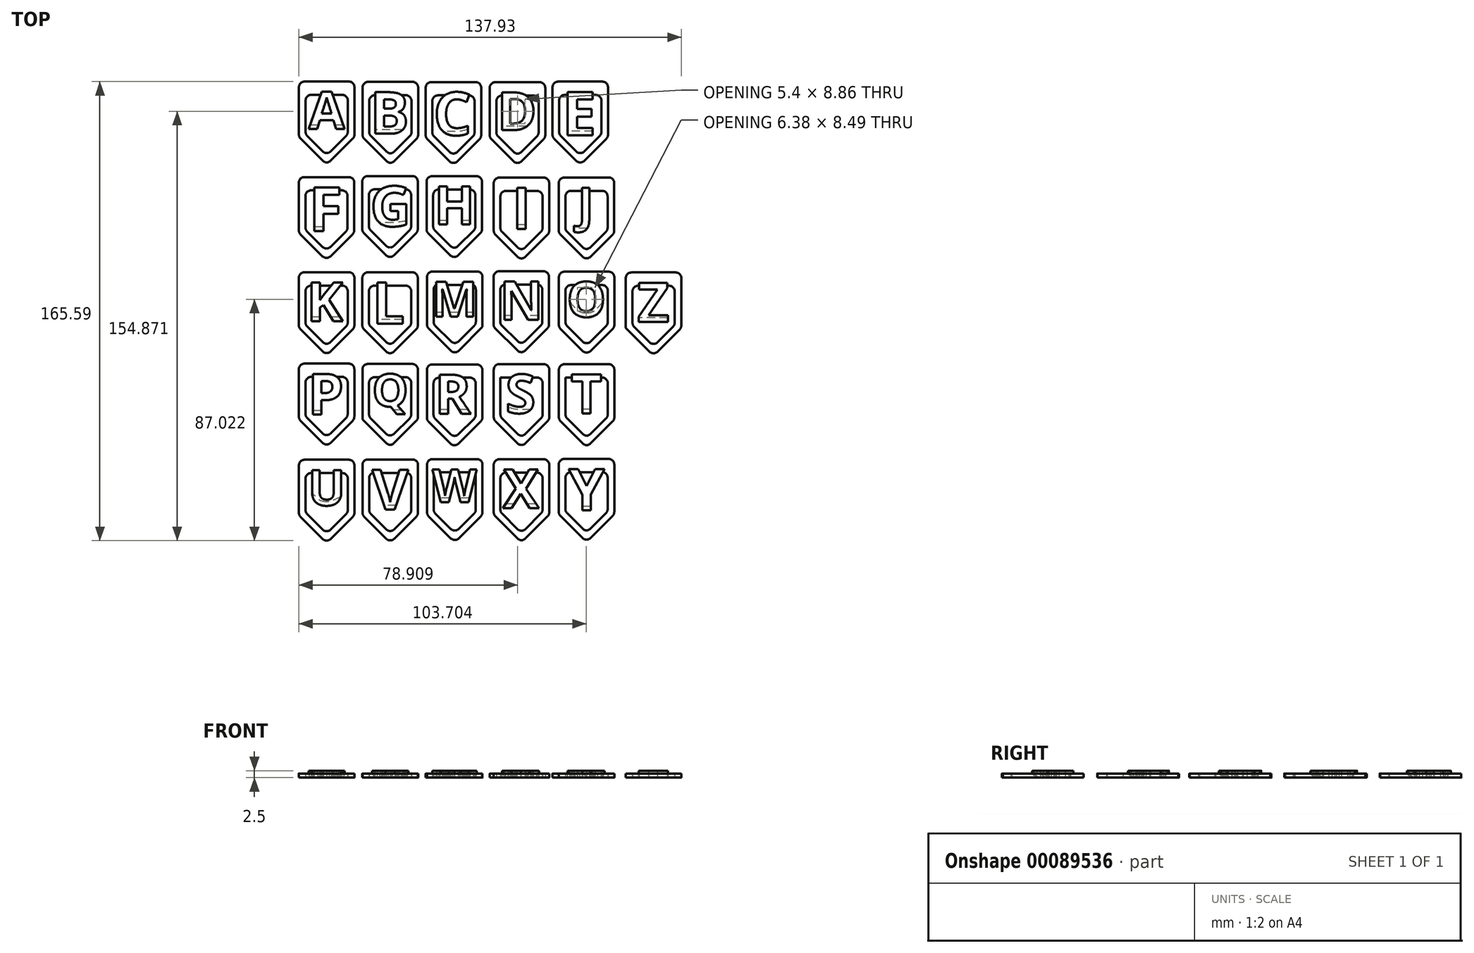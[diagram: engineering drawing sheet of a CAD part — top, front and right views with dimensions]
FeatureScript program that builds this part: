
annotation { "Feature Type Name" : "Feature", "Feature Type Description" : "" }
export const myFeature = defineFeature(function(context is Context, id is Id, definition is map)
    precondition{}
    {
        {
            assignVariable(context, id + "F0", {"name" : "ClipWidth", "anyValue" : 1.5});
        }
        {
            assignVariable(context, id + "F1", {"name" : "LetterWidth", "anyValue" : 2.5});
        }
        {
            var Q0;
            Q0=qCreatedBy(makeId("Top.planeOp"),FACE);
            var sketch = newSketch(context, id + "F2", { "sketchPlane" : qUnion([Q0])});
            skLineSegment(sketch, "E0", {"start": v(-68.8, 39.05) * mm, "end": v(-48.8, 39.05) * mm});
            skLineSegment(sketch, "E1", {"start": v(-48.8, 39.05) * mm, "end": v(-48.8, 19.05) * mm});
            skLineSegment(sketch, "E2", {"start": v(-48.8, 19.05) * mm, "end": v(-58.8, 9.05) * mm});
            skPoint(sketch, "E2.endSnap0", {"position": v(-58.8, 39.05) * mm});
            skLineSegment(sketch, "E3", {"start": v(-58.8, 9.05) * mm, "end": v(-68.8, 19.05) * mm});
            skLineSegment(sketch, "E4", {"start": v(-68.8, 19.05) * mm, "end": v(-68.8, 39.05) * mm});
            skLineSegment(sketch, "E5", {"start": v(-66.4, 34.25) * mm, "end": v(-51.2, 34.25) * mm});
            skLineSegment(sketch, "E6", {"start": v(-51.2, 34.25) * mm, "end": v(-51.2, 20.05) * mm});
            skLineSegment(sketch, "E7", {"start": v(-51.2, 20.05) * mm, "end": v(-58.8, 12.45) * mm});
            skLineSegment(sketch, "E8", {"start": v(-58.8, 12.45) * mm, "end": v(-66.4, 20.05) * mm});
            skLineSegment(sketch, "E9", {"start": v(-66.4, 20.05) * mm, "end": v(-66.4, 34.25) * mm});
            skText(sketch, "E10", { "text": "A", "fontName": "OpenSans-Bold.ttf"});
            skLineSegment(sketch, "E11", {"start": v(-58.8, 27.15) * mm, "end": v(-58.8, 43.75) * mm, "construction": true});
            const initialGuessF2  = {"E10": [-0.0653, 0.02189, 1, 0, 0.01357]};
            skSetInitialGuess(sketch, initialGuessF2);
            skSolve(sketch);
        }
        {
            var Q0;
            Q0=qCreatedBy(makeId("Top.planeOp"),FACE);
            var sketch = newSketch(context, id + "F3", { "sketchPlane" : qUnion([Q0])});
            skLineSegment(sketch, "E12", {"start": v(-45.83, 38.94) * mm, "end": v(-25.83, 38.94) * mm});
            skLineSegment(sketch, "E13", {"start": v(-25.83, 38.94) * mm, "end": v(-25.83, 18.94) * mm});
            skLineSegment(sketch, "E14", {"start": v(-25.83, 18.94) * mm, "end": v(-35.83, 8.94) * mm});
            skPoint(sketch, "E14.endSnap0", {"position": v(-35.83, 38.94) * mm});
            skLineSegment(sketch, "E15", {"start": v(-35.83, 8.94) * mm, "end": v(-45.83, 18.94) * mm});
            skLineSegment(sketch, "E16", {"start": v(-45.83, 18.94) * mm, "end": v(-45.83, 38.94) * mm});
            skLineSegment(sketch, "E17", {"start": v(-43.43, 34.14) * mm, "end": v(-28.23, 34.14) * mm});
            skLineSegment(sketch, "E18", {"start": v(-28.23, 34.14) * mm, "end": v(-28.23, 19.94) * mm});
            skLineSegment(sketch, "E19", {"start": v(-28.23, 19.94) * mm, "end": v(-35.83, 12.34) * mm});
            skLineSegment(sketch, "E20", {"start": v(-35.83, 12.34) * mm, "end": v(-43.43, 19.94) * mm});
            skLineSegment(sketch, "E21", {"start": v(-43.43, 19.94) * mm, "end": v(-43.43, 34.14) * mm});
            skText(sketch, "E22", { "text": "B", "fontName": "OpenSans-Bold.ttf"});
            skLineSegment(sketch, "E23", {"start": v(-35.83, 31.44) * mm, "end": v(-35.83, 39.25) * mm, "construction": true});
            const initialGuessF3  = {"E22": [-0.04323, 0.02023, 1, 0, 0.01512]};
            skSetInitialGuess(sketch, initialGuessF3);
            skSolve(sketch);
        }
        {
            var Q0;
            Q0=qCreatedBy(makeId("Top.planeOp"),FACE);
            var sketch = newSketch(context, id + "F4", { "sketchPlane" : qUnion([Q0])});
            skLineSegment(sketch, "E24", {"start": v(-23.1, 38.87) * mm, "end": v(-3.1, 38.87) * mm});
            skLineSegment(sketch, "E25", {"start": v(-3.1, 38.87) * mm, "end": v(-3.1, 18.87) * mm});
            skLineSegment(sketch, "E26", {"start": v(-3.1, 18.87) * mm, "end": v(-13.1, 8.87) * mm});
            skPoint(sketch, "E26.endSnap0", {"position": v(-13.1, 38.87) * mm});
            skLineSegment(sketch, "E27", {"start": v(-13.1, 8.87) * mm, "end": v(-23.1, 18.87) * mm});
            skLineSegment(sketch, "E28", {"start": v(-23.1, 18.87) * mm, "end": v(-23.1, 38.87) * mm});
            skLineSegment(sketch, "E29", {"start": v(-20.7, 34.07) * mm, "end": v(-5.5, 34.07) * mm});
            skLineSegment(sketch, "E30", {"start": v(-5.5, 34.07) * mm, "end": v(-5.5, 19.86) * mm});
            skLineSegment(sketch, "E31", {"start": v(-5.5, 19.86) * mm, "end": v(-13.1, 12.26) * mm});
            skLineSegment(sketch, "E32", {"start": v(-13.1, 12.26) * mm, "end": v(-20.7, 19.86) * mm});
            skLineSegment(sketch, "E33", {"start": v(-20.7, 19.86) * mm, "end": v(-20.7, 34.07) * mm});
            skText(sketch, "E34", { "text": "C", "fontName": "OpenSans-Bold.ttf"});
            skLineSegment(sketch, "E35", {"start": v(-13.1, 13.29) * mm, "end": v(-13.1, 57.25) * mm, "construction": true});
            const initialGuessF4  = {"E34": [-0.02035, 0.01972, 1, 0, 0.01555]};
            skSetInitialGuess(sketch, initialGuessF4);
            skSolve(sketch);
        }
        {
            var Q0;
            Q0=qCreatedBy(makeId("Top.planeOp"),FACE);
            var sketch = newSketch(context, id + "F5", { "sketchPlane" : qUnion([Q0])});
            skLineSegment(sketch, "E36", {"start": v(0, 38.85) * mm, "end": v(20, 38.85) * mm});
            skLineSegment(sketch, "E37", {"start": v(20, 38.85) * mm, "end": v(20, 18.85) * mm});
            skLineSegment(sketch, "E38", {"start": v(20, 18.85) * mm, "end": v(10, 8.85) * mm});
            skPoint(sketch, "E38.endSnap0", {"position": v(10, 38.85) * mm});
            skLineSegment(sketch, "E39", {"start": v(10, 8.85) * mm, "end": v(0, 18.85) * mm});
            skLineSegment(sketch, "E40", {"start": v(0, 18.85) * mm, "end": v(0, 38.85) * mm});
            skLineSegment(sketch, "E41", {"start": v(2.4, 34.05) * mm, "end": v(17.6, 34.05) * mm});
            skLineSegment(sketch, "E42", {"start": v(17.6, 34.05) * mm, "end": v(17.6, 19.84) * mm});
            skLineSegment(sketch, "E43", {"start": v(17.6, 19.84) * mm, "end": v(10, 12.24) * mm});
            skLineSegment(sketch, "E44", {"start": v(10, 12.24) * mm, "end": v(2.4, 19.84) * mm});
            skLineSegment(sketch, "E45", {"start": v(2.4, 19.84) * mm, "end": v(2.4, 34.05) * mm});
            skText(sketch, "E46", { "text": "D", "fontName": "OpenSans-Bold.ttf"});
            skLineSegment(sketch, "E47", {"start": v(10, 0.42) * mm, "end": v(10, 70.07) * mm, "construction": true});
            const initialGuessF5  = {"E46": [0.00275, 0.02152, 1, 0, 0.01372]};
            skSetInitialGuess(sketch, initialGuessF5);
            skSolve(sketch);
        }
        {
            var Q0;
            Q0=qCreatedBy(makeId("Top.planeOp"),FACE);
            var sketch = newSketch(context, id + "F6", { "sketchPlane" : qUnion([Q0])});
            skLineSegment(sketch, "E48", {"start": v(22.63, 39.03) * mm, "end": v(42.63, 39.03) * mm});
            skLineSegment(sketch, "E49", {"start": v(42.63, 39.03) * mm, "end": v(42.63, 19.03) * mm});
            skLineSegment(sketch, "E50", {"start": v(42.63, 19.03) * mm, "end": v(32.63, 9.03) * mm});
            skPoint(sketch, "E50.endSnap0", {"position": v(32.63, 39.03) * mm});
            skLineSegment(sketch, "E51", {"start": v(32.63, 9.03) * mm, "end": v(22.63, 19.03) * mm});
            skLineSegment(sketch, "E52", {"start": v(22.63, 19.03) * mm, "end": v(22.63, 39.03) * mm});
            skLineSegment(sketch, "E53", {"start": v(25.03, 34.23) * mm, "end": v(40.23, 34.23) * mm});
            skLineSegment(sketch, "E54", {"start": v(40.23, 34.23) * mm, "end": v(40.23, 20.02) * mm});
            skLineSegment(sketch, "E55", {"start": v(40.23, 20.02) * mm, "end": v(32.63, 12.42) * mm});
            skLineSegment(sketch, "E56", {"start": v(32.63, 12.42) * mm, "end": v(25.03, 20.02) * mm});
            skLineSegment(sketch, "E57", {"start": v(25.03, 20.02) * mm, "end": v(25.03, 34.23) * mm});
            skText(sketch, "E58", { "text": "E", "fontName": "OpenSans-Bold.ttf"});
            skLineSegment(sketch, "E59", {"start": v(32.63, 0.42) * mm, "end": v(32.63, 70.43) * mm, "construction": true});
            const initialGuessF6  = {"E58": [0.02614, 0.01962, 1, 0, 0.01581]};
            skSetInitialGuess(sketch, initialGuessF6);
            skSolve(sketch);
        }
        {
            var Q0;
            Q0=qCreatedBy(makeId("Top.planeOp"),FACE);
            var sketch = newSketch(context, id + "F7", { "sketchPlane" : qUnion([Q0])});
            skLineSegment(sketch, "E60", {"start": v(-68.86, 4.6) * mm, "end": v(-48.86, 4.6) * mm});
            skLineSegment(sketch, "E61", {"start": v(-48.86, 4.6) * mm, "end": v(-48.86, -15.4) * mm});
            skLineSegment(sketch, "E62", {"start": v(-48.86, -15.4) * mm, "end": v(-58.86, -25.4) * mm});
            skPoint(sketch, "E62.endSnap0", {"position": v(-58.86, 4.6) * mm});
            skLineSegment(sketch, "E63", {"start": v(-58.86, -25.4) * mm, "end": v(-68.86, -15.4) * mm});
            skLineSegment(sketch, "E64", {"start": v(-68.86, -15.4) * mm, "end": v(-68.86, 4.6) * mm});
            skLineSegment(sketch, "E65", {"start": v(-66.46, -0.2) * mm, "end": v(-51.26, -0.2) * mm});
            skLineSegment(sketch, "E66", {"start": v(-51.26, -0.2) * mm, "end": v(-51.26, -14.4) * mm});
            skLineSegment(sketch, "E67", {"start": v(-51.26, -14.4) * mm, "end": v(-58.86, -22) * mm});
            skLineSegment(sketch, "E68", {"start": v(-58.86, -22) * mm, "end": v(-66.46, -14.4) * mm});
            skLineSegment(sketch, "E69", {"start": v(-66.46, -14.4) * mm, "end": v(-66.46, -0.2) * mm});
            skText(sketch, "E70", { "text": "F", "fontName": "OpenSans-Bold.ttf"});
            skLineSegment(sketch, "E71", {"start": v(-58.86, -29.54) * mm, "end": v(-58.86, 31.53) * mm, "construction": true});
            const initialGuessF7  = {"E70": [-0.0652, -0.01487, 1, 0, 0.01587]};
            skSetInitialGuess(sketch, initialGuessF7);
            skSolve(sketch);
        }
        {
            var Q0;
            Q0=qCreatedBy(makeId("Top.planeOp"),FACE);
            var sketch = newSketch(context, id + "F8", { "sketchPlane" : qUnion([Q0])});
            skLineSegment(sketch, "E72", {"start": v(-45.95, 4.98) * mm, "end": v(-25.95, 4.98) * mm});
            skLineSegment(sketch, "E73", {"start": v(-25.95, 4.98) * mm, "end": v(-25.95, -15.02) * mm});
            skLineSegment(sketch, "E74", {"start": v(-25.95, -15.02) * mm, "end": v(-35.95, -25.02) * mm});
            skPoint(sketch, "E74.endSnap0", {"position": v(-35.95, 4.98) * mm});
            skLineSegment(sketch, "E75", {"start": v(-35.95, -25.02) * mm, "end": v(-45.95, -15.02) * mm});
            skLineSegment(sketch, "E76", {"start": v(-45.95, -15.02) * mm, "end": v(-45.95, 4.98) * mm});
            skLineSegment(sketch, "E77", {"start": v(-43.55, 0.18) * mm, "end": v(-28.35, 0.18) * mm});
            skLineSegment(sketch, "E78", {"start": v(-28.35, 0.18) * mm, "end": v(-28.35, -14.02) * mm});
            skLineSegment(sketch, "E79", {"start": v(-28.35, -14.02) * mm, "end": v(-35.95, -21.62) * mm});
            skLineSegment(sketch, "E80", {"start": v(-35.95, -21.62) * mm, "end": v(-43.55, -14.02) * mm});
            skLineSegment(sketch, "E81", {"start": v(-43.55, -14.02) * mm, "end": v(-43.55, 0.18) * mm});
            skText(sketch, "E82", { "text": "G", "fontName": "OpenSans-Bold.ttf"});
            skLineSegment(sketch, "E83", {"start": v(-35.95, -0.1) * mm, "end": v(-35.95, 2.87) * mm, "construction": true});
            const initialGuessF8  = {"E82": [-0.0431, -0.01315, 1, 0, 0.01453]};
            skSetInitialGuess(sketch, initialGuessF8);
            skSolve(sketch);
        }
        {
            var Q0;
            Q0=qCreatedBy(makeId("Top.planeOp"),FACE);
            var sketch = newSketch(context, id + "F9", { "sketchPlane" : qUnion([Q0])});
            skLineSegment(sketch, "E84", {"start": v(-22.8, 4.94) * mm, "end": v(-2.8, 4.94) * mm});
            skLineSegment(sketch, "E85", {"start": v(-2.8, 4.94) * mm, "end": v(-2.8, -15.06) * mm});
            skLineSegment(sketch, "E86", {"start": v(-2.8, -15.06) * mm, "end": v(-12.8, -25.06) * mm});
            skPoint(sketch, "E86.endSnap0", {"position": v(-12.8, 4.94) * mm});
            skLineSegment(sketch, "E87", {"start": v(-12.8, -25.06) * mm, "end": v(-22.8, -15.06) * mm});
            skLineSegment(sketch, "E88", {"start": v(-22.8, -15.06) * mm, "end": v(-22.8, 4.94) * mm});
            skLineSegment(sketch, "E89", {"start": v(-20.4, 0.14) * mm, "end": v(-5.2, 0.14) * mm});
            skLineSegment(sketch, "E90", {"start": v(-5.2, 0.14) * mm, "end": v(-5.2, -14.07) * mm});
            skLineSegment(sketch, "E91", {"start": v(-5.2, -14.07) * mm, "end": v(-12.8, -21.67) * mm});
            skLineSegment(sketch, "E92", {"start": v(-12.8, -21.67) * mm, "end": v(-20.4, -14.07) * mm});
            skLineSegment(sketch, "E93", {"start": v(-20.4, -14.07) * mm, "end": v(-20.4, 0.14) * mm});
            skText(sketch, "E94", { "text": "H", "fontName": "OpenSans-Bold.ttf"});
            skLineSegment(sketch, "E95", {"start": v(-12.8, 0.84) * mm, "end": v(-12.8, 1.84) * mm, "construction": true});
            const initialGuessF9  = {"E94": [-0.02007, -0.01253, 1, 0, 0.01387]};
            skSetInitialGuess(sketch, initialGuessF9);
            skSolve(sketch);
        }
        {
            var Q0;
            Q0=qCreatedBy(makeId("Top.planeOp"),FACE);
            var sketch = newSketch(context, id + "F10", { "sketchPlane" : qUnion([Q0])});
            skLineSegment(sketch, "E96", {"start": v(1.43, 4.42) * mm, "end": v(21.43, 4.42) * mm});
            skLineSegment(sketch, "E97", {"start": v(21.43, 4.42) * mm, "end": v(21.43, -15.58) * mm});
            skLineSegment(sketch, "E98", {"start": v(21.43, -15.58) * mm, "end": v(11.43, -25.58) * mm});
            skPoint(sketch, "E98.endSnap0", {"position": v(11.43, 4.42) * mm});
            skLineSegment(sketch, "E99", {"start": v(11.43, -25.58) * mm, "end": v(1.43, -15.58) * mm});
            skLineSegment(sketch, "E100", {"start": v(1.43, -15.58) * mm, "end": v(1.43, 4.42) * mm});
            skLineSegment(sketch, "E101", {"start": v(3.83, -0.38) * mm, "end": v(19.03, -0.38) * mm});
            skLineSegment(sketch, "E102", {"start": v(19.03, -0.38) * mm, "end": v(19.03, -14.59) * mm});
            skLineSegment(sketch, "E103", {"start": v(19.03, -14.59) * mm, "end": v(11.43, -22.19) * mm});
            skLineSegment(sketch, "E104", {"start": v(11.43, -22.19) * mm, "end": v(3.83, -14.59) * mm});
            skLineSegment(sketch, "E105", {"start": v(3.83, -14.59) * mm, "end": v(3.83, -0.38) * mm});
            skText(sketch, "E106", { "text": "I", "fontName": "OpenSans-Bold.ttf"});
            skLineSegment(sketch, "E107", {"start": v(11.43, -0.98) * mm, "end": v(11.43, 3.5) * mm, "construction": true});
            const initialGuessF10  = {"E106": [0.00798, -0.0141, 1, 0, 0.01492]};
            skSetInitialGuess(sketch, initialGuessF10);
            skSolve(sketch);
        }
        {
            var Q0;
            Q0=qCreatedBy(makeId("Top.planeOp"),FACE);
            var sketch = newSketch(context, id + "F11", { "sketchPlane" : qUnion([Q0])});
            skLineSegment(sketch, "E108", {"start": v(24.89, 4.45) * mm, "end": v(44.89, 4.45) * mm});
            skLineSegment(sketch, "E109", {"start": v(44.89, 4.45) * mm, "end": v(44.89, -15.55) * mm});
            skLineSegment(sketch, "E110", {"start": v(44.89, -15.55) * mm, "end": v(34.89, -25.55) * mm});
            skPoint(sketch, "E110.endSnap0", {"position": v(34.89, 4.45) * mm});
            skLineSegment(sketch, "E111", {"start": v(34.89, -25.55) * mm, "end": v(24.89, -15.55) * mm});
            skLineSegment(sketch, "E112", {"start": v(24.89, -15.55) * mm, "end": v(24.89, 4.45) * mm});
            skLineSegment(sketch, "E113", {"start": v(27.29, -0.35) * mm, "end": v(42.49, -0.35) * mm});
            skLineSegment(sketch, "E114", {"start": v(42.49, -0.35) * mm, "end": v(42.49, -14.55) * mm});
            skLineSegment(sketch, "E115", {"start": v(42.49, -14.55) * mm, "end": v(34.89, -22.15) * mm});
            skLineSegment(sketch, "E116", {"start": v(34.89, -22.15) * mm, "end": v(27.29, -14.55) * mm});
            skLineSegment(sketch, "E117", {"start": v(27.29, -14.55) * mm, "end": v(27.29, -0.35) * mm});
            skText(sketch, "E118", { "text": "J", "fontName": "OpenSans-Bold.ttf"});
            skLineSegment(sketch, "E119", {"start": v(34.89, -5.18) * mm, "end": v(34.89, 6.88) * mm, "construction": true});
            const initialGuessF11  = {"E118": [0.03168, -0.0117, 1, 0, 0.01255]};
            skSetInitialGuess(sketch, initialGuessF11);
            skSolve(sketch);
        }
        {
            var Q0;
            Q0=qCreatedBy(makeId("Top.planeOp"),FACE);
            var sketch = newSketch(context, id + "F12", { "sketchPlane" : qUnion([Q0])});
            skLineSegment(sketch, "E120", {"start": v(-68.82, -29.73) * mm, "end": v(-48.82, -29.73) * mm});
            skLineSegment(sketch, "E121", {"start": v(-48.82, -29.73) * mm, "end": v(-48.82, -49.73) * mm});
            skLineSegment(sketch, "E122", {"start": v(-48.82, -49.73) * mm, "end": v(-58.82, -59.73) * mm});
            skPoint(sketch, "E122.endSnap0", {"position": v(-58.82, -29.73) * mm});
            skLineSegment(sketch, "E123", {"start": v(-58.82, -59.73) * mm, "end": v(-68.82, -49.73) * mm});
            skLineSegment(sketch, "E124", {"start": v(-68.82, -49.73) * mm, "end": v(-68.82, -29.73) * mm});
            skLineSegment(sketch, "E125", {"start": v(-66.42, -34.53) * mm, "end": v(-51.22, -34.53) * mm});
            skLineSegment(sketch, "E126", {"start": v(-51.22, -34.53) * mm, "end": v(-51.22, -48.73) * mm});
            skLineSegment(sketch, "E127", {"start": v(-51.22, -48.73) * mm, "end": v(-58.82, -56.33) * mm});
            skLineSegment(sketch, "E128", {"start": v(-58.82, -56.33) * mm, "end": v(-66.42, -48.73) * mm});
            skLineSegment(sketch, "E129", {"start": v(-66.42, -48.73) * mm, "end": v(-66.42, -34.53) * mm});
            skText(sketch, "E130", { "text": "K", "fontName": "OpenSans-Bold.ttf"});
            skLineSegment(sketch, "E131", {"start": v(-58.82, -47.23) * mm, "end": v(-58.82, -19.43) * mm, "construction": true});
            const initialGuessF12  = {"E130": [-0.06598, -0.04742, 1, 0, 0.0141]};
            skSetInitialGuess(sketch, initialGuessF12);
            skSolve(sketch);
        }
        {
            var Q0;
            Q0=qCreatedBy(makeId("Top.planeOp"),FACE);
            var sketch = newSketch(context, id + "F13", { "sketchPlane" : qUnion([Q0])});
            skLineSegment(sketch, "E132", {"start": v(-45.94, -29.75) * mm, "end": v(-25.94, -29.75) * mm});
            skLineSegment(sketch, "E133", {"start": v(-25.94, -29.75) * mm, "end": v(-25.94, -49.75) * mm});
            skLineSegment(sketch, "E134", {"start": v(-25.94, -49.75) * mm, "end": v(-35.94, -59.75) * mm});
            skPoint(sketch, "E134.endSnap0", {"position": v(-35.94, -29.75) * mm});
            skLineSegment(sketch, "E135", {"start": v(-35.94, -59.75) * mm, "end": v(-45.94, -49.75) * mm});
            skLineSegment(sketch, "E136", {"start": v(-45.94, -49.75) * mm, "end": v(-45.94, -29.75) * mm});
            skLineSegment(sketch, "E137", {"start": v(-43.54, -34.55) * mm, "end": v(-28.34, -34.55) * mm});
            skLineSegment(sketch, "E138", {"start": v(-28.34, -34.55) * mm, "end": v(-28.34, -48.76) * mm});
            skLineSegment(sketch, "E139", {"start": v(-28.34, -48.76) * mm, "end": v(-35.94, -56.36) * mm});
            skLineSegment(sketch, "E140", {"start": v(-35.94, -56.36) * mm, "end": v(-43.54, -48.76) * mm});
            skLineSegment(sketch, "E141", {"start": v(-43.54, -48.76) * mm, "end": v(-43.54, -34.55) * mm});
            skText(sketch, "E142", { "text": "L", "fontName": "OpenSans-Bold.ttf"});
            skLineSegment(sketch, "E143", {"start": v(-35.94, -40.7) * mm, "end": v(-35.94, -26) * mm, "construction": true});
            const initialGuessF13  = {"E142": [-0.04236, -0.04827, 1, 0, 0.01492]};
            skSetInitialGuess(sketch, initialGuessF13);
            skSolve(sketch);
        }
        {
            var Q0;
            Q0=qCreatedBy(makeId("Top.planeOp"),FACE);
            var sketch = newSketch(context, id + "F14", { "sketchPlane" : qUnion([Q0])});
            skLineSegment(sketch, "E144", {"start": v(-22.62, -29.46) * mm, "end": v(-2.62, -29.46) * mm});
            skLineSegment(sketch, "E145", {"start": v(-2.62, -29.46) * mm, "end": v(-2.62, -49.46) * mm});
            skLineSegment(sketch, "E146", {"start": v(-2.62, -49.46) * mm, "end": v(-12.62, -59.46) * mm});
            skPoint(sketch, "E146.endSnap0", {"position": v(-12.62, -29.46) * mm});
            skLineSegment(sketch, "E147", {"start": v(-12.62, -59.46) * mm, "end": v(-22.62, -49.46) * mm});
            skLineSegment(sketch, "E148", {"start": v(-22.62, -49.46) * mm, "end": v(-22.62, -29.46) * mm});
            skLineSegment(sketch, "E149", {"start": v(-20.22, -34.26) * mm, "end": v(-5.02, -34.26) * mm});
            skLineSegment(sketch, "E150", {"start": v(-5.02, -34.26) * mm, "end": v(-5.02, -48.46) * mm});
            skLineSegment(sketch, "E151", {"start": v(-5.02, -48.46) * mm, "end": v(-12.62, -56.06) * mm});
            skLineSegment(sketch, "E152", {"start": v(-12.62, -56.06) * mm, "end": v(-20.22, -48.46) * mm});
            skLineSegment(sketch, "E153", {"start": v(-20.22, -48.46) * mm, "end": v(-20.22, -34.26) * mm});
            skText(sketch, "E154", { "text": "M", "fontName": "OpenSans-Bold.ttf"});
            skLineSegment(sketch, "E155", {"start": v(-12.62, -42.78) * mm, "end": v(-12.62, -23.34) * mm, "construction": true});
            const initialGuessF14  = {"E154": [-0.02094, -0.04572, 1, 0, 0.01266]};
            skSetInitialGuess(sketch, initialGuessF14);
            skSolve(sketch);
        }
        {
            var Q0;
            Q0=qCreatedBy(makeId("Top.planeOp"),FACE);
            var sketch = newSketch(context, id + "F15", { "sketchPlane" : qUnion([Q0])});
            skLineSegment(sketch, "E156", {"start": v(1.38, -29.38) * mm, "end": v(21.38, -29.38) * mm});
            skLineSegment(sketch, "E157", {"start": v(21.38, -29.38) * mm, "end": v(21.38, -49.38) * mm});
            skLineSegment(sketch, "E158", {"start": v(21.38, -49.38) * mm, "end": v(11.38, -59.38) * mm});
            skPoint(sketch, "E158.endSnap0", {"position": v(11.38, -29.38) * mm});
            skLineSegment(sketch, "E159", {"start": v(11.38, -59.38) * mm, "end": v(1.38, -49.38) * mm});
            skLineSegment(sketch, "E160", {"start": v(1.38, -49.38) * mm, "end": v(1.38, -29.38) * mm});
            skLineSegment(sketch, "E161", {"start": v(3.78, -34.18) * mm, "end": v(18.98, -34.18) * mm});
            skLineSegment(sketch, "E162", {"start": v(18.98, -34.18) * mm, "end": v(18.98, -48.38) * mm});
            skLineSegment(sketch, "E163", {"start": v(18.98, -48.38) * mm, "end": v(11.38, -55.98) * mm});
            skLineSegment(sketch, "E164", {"start": v(11.38, -55.98) * mm, "end": v(3.78, -48.38) * mm});
            skLineSegment(sketch, "E165", {"start": v(3.78, -48.38) * mm, "end": v(3.78, -34.18) * mm});
            skText(sketch, "E166", { "text": "N", "fontName": "OpenSans-Bold.ttf"});
            skLineSegment(sketch, "E167", {"start": v(11.38, -50.26) * mm, "end": v(11.38, -15.7) * mm, "construction": true});
            const initialGuessF15  = {"E166": [0.00354, -0.04691, 1, 0, 0.01394]};
            skSetInitialGuess(sketch, initialGuessF15);
            skSolve(sketch);
        }
        {
            var Q0;
            Q0=qCreatedBy(makeId("Top.planeOp"),FACE);
            var sketch = newSketch(context, id + "F16", { "sketchPlane" : qUnion([Q0])});
            skLineSegment(sketch, "E168", {"start": v(24.92, -29.55) * mm, "end": v(44.92, -29.55) * mm});
            skLineSegment(sketch, "E169", {"start": v(44.92, -29.55) * mm, "end": v(44.92, -49.55) * mm});
            skLineSegment(sketch, "E170", {"start": v(44.92, -49.55) * mm, "end": v(34.92, -59.55) * mm});
            skPoint(sketch, "E170.endSnap0", {"position": v(34.92, -29.55) * mm});
            skLineSegment(sketch, "E171", {"start": v(34.92, -59.55) * mm, "end": v(24.92, -49.55) * mm});
            skLineSegment(sketch, "E172", {"start": v(24.92, -49.55) * mm, "end": v(24.92, -29.55) * mm});
            skLineSegment(sketch, "E173", {"start": v(27.32, -34.35) * mm, "end": v(42.52, -34.35) * mm});
            skLineSegment(sketch, "E174", {"start": v(42.52, -34.35) * mm, "end": v(42.52, -48.55) * mm});
            skLineSegment(sketch, "E175", {"start": v(42.52, -48.55) * mm, "end": v(34.92, -56.15) * mm});
            skLineSegment(sketch, "E176", {"start": v(34.92, -56.15) * mm, "end": v(27.32, -48.55) * mm});
            skLineSegment(sketch, "E177", {"start": v(27.32, -48.55) * mm, "end": v(27.32, -34.35) * mm});
            skText(sketch, "E178", { "text": "O", "fontName": "OpenSans-Bold.ttf"});
            skLineSegment(sketch, "E179", {"start": v(34.92, -52.38) * mm, "end": v(34.92, -13.92) * mm, "construction": true});
            const initialGuessF16  = {"E178": [0.02783, -0.04583, 1, 0, 0.01269]};
            skSetInitialGuess(sketch, initialGuessF16);
            skSolve(sketch);
        }
        {
            var Q0;
            Q0=qCreatedBy(makeId("Top.planeOp"),FACE);
            var sketch = newSketch(context, id + "F17", { "sketchPlane" : qUnion([Q0])});
            skLineSegment(sketch, "E180", {"start": v(-68.83, -62.7) * mm, "end": v(-48.83, -62.7) * mm});
            skLineSegment(sketch, "E181", {"start": v(-48.83, -62.7) * mm, "end": v(-48.83, -82.7) * mm});
            skLineSegment(sketch, "E182", {"start": v(-48.83, -82.7) * mm, "end": v(-58.83, -92.7) * mm});
            skPoint(sketch, "E182.endSnap0", {"position": v(-58.83, -62.7) * mm});
            skLineSegment(sketch, "E183", {"start": v(-58.83, -92.7) * mm, "end": v(-68.83, -82.7) * mm});
            skLineSegment(sketch, "E184", {"start": v(-68.83, -82.7) * mm, "end": v(-68.83, -62.7) * mm});
            skLineSegment(sketch, "E185", {"start": v(-66.43, -67.5) * mm, "end": v(-51.23, -67.5) * mm});
            skLineSegment(sketch, "E186", {"start": v(-51.23, -67.5) * mm, "end": v(-51.23, -81.7) * mm});
            skLineSegment(sketch, "E187", {"start": v(-51.23, -81.7) * mm, "end": v(-58.83, -89.3) * mm});
            skLineSegment(sketch, "E188", {"start": v(-58.83, -89.3) * mm, "end": v(-66.43, -81.7) * mm});
            skLineSegment(sketch, "E189", {"start": v(-66.43, -81.7) * mm, "end": v(-66.43, -67.5) * mm});
            skText(sketch, "E190", { "text": "P", "fontName": "OpenSans-Bold.ttf"});
            skLineSegment(sketch, "E191", {"start": v(-58.83, -82.94) * mm, "end": v(-58.83, -49.65) * mm, "construction": true});
            const initialGuessF17  = {"E190": [-0.06562, -0.08111, 1, 0, 0.01482]};
            skSetInitialGuess(sketch, initialGuessF17);
            skSolve(sketch);
        }
        {
            var Q0;
            Q0=qCreatedBy(makeId("Top.planeOp"),FACE);
            var sketch = newSketch(context, id + "F18", { "sketchPlane" : qUnion([Q0])});
            skLineSegment(sketch, "E192", {"start": v(-45.91, -62.8) * mm, "end": v(-25.91, -62.8) * mm});
            skLineSegment(sketch, "E193", {"start": v(-25.91, -62.8) * mm, "end": v(-25.91, -82.8) * mm});
            skLineSegment(sketch, "E194", {"start": v(-25.91, -82.8) * mm, "end": v(-35.91, -92.8) * mm});
            skPoint(sketch, "E194.endSnap0", {"position": v(-35.91, -62.8) * mm});
            skLineSegment(sketch, "E195", {"start": v(-35.91, -92.8) * mm, "end": v(-45.91, -82.8) * mm});
            skLineSegment(sketch, "E196", {"start": v(-45.91, -82.8) * mm, "end": v(-45.91, -62.8) * mm});
            skLineSegment(sketch, "E197", {"start": v(-43.51, -67.6) * mm, "end": v(-28.31, -67.6) * mm});
            skLineSegment(sketch, "E198", {"start": v(-28.31, -67.6) * mm, "end": v(-28.31, -81.82) * mm});
            skLineSegment(sketch, "E199", {"start": v(-28.31, -81.82) * mm, "end": v(-35.91, -89.42) * mm});
            skLineSegment(sketch, "E200", {"start": v(-35.91, -89.42) * mm, "end": v(-43.51, -81.82) * mm});
            skLineSegment(sketch, "E201", {"start": v(-43.51, -81.82) * mm, "end": v(-43.51, -67.6) * mm});
            skText(sketch, "E202", { "text": "Q", "fontName": "OpenSans-Bold.ttf"});
            skLineSegment(sketch, "E203", {"start": v(-35.91, -81.8) * mm, "end": v(-35.91, -51.02) * mm, "construction": true});
            const initialGuessF18  = {"E202": [-0.04237, -0.07812, 1, 0, 0.01171]};
            skSetInitialGuess(sketch, initialGuessF18);
            skSolve(sketch);
        }
        {
            var Q0;
            Q0=qCreatedBy(makeId("Top.planeOp"),FACE);
            var sketch = newSketch(context, id + "F19", { "sketchPlane" : qUnion([Q0])});
            skLineSegment(sketch, "E204", {"start": v(-22.67, -62.97) * mm, "end": v(-2.67, -62.97) * mm});
            skLineSegment(sketch, "E205", {"start": v(-2.67, -62.97) * mm, "end": v(-2.67, -82.97) * mm});
            skLineSegment(sketch, "E206", {"start": v(-2.67, -82.97) * mm, "end": v(-12.67, -92.97) * mm});
            skPoint(sketch, "E206.endSnap0", {"position": v(-12.67, -62.97) * mm});
            skLineSegment(sketch, "E207", {"start": v(-12.67, -92.97) * mm, "end": v(-22.67, -82.97) * mm});
            skLineSegment(sketch, "E208", {"start": v(-22.67, -82.97) * mm, "end": v(-22.67, -62.97) * mm});
            skLineSegment(sketch, "E209", {"start": v(-20.27, -67.77) * mm, "end": v(-5.07, -67.77) * mm});
            skLineSegment(sketch, "E210", {"start": v(-5.07, -67.77) * mm, "end": v(-5.07, -81.98) * mm});
            skLineSegment(sketch, "E211", {"start": v(-5.07, -81.98) * mm, "end": v(-12.67, -89.58) * mm});
            skLineSegment(sketch, "E212", {"start": v(-12.67, -89.58) * mm, "end": v(-20.27, -81.98) * mm});
            skLineSegment(sketch, "E213", {"start": v(-20.27, -81.98) * mm, "end": v(-20.27, -67.77) * mm});
            skText(sketch, "E214", { "text": "R", "fontName": "OpenSans-Bold.ttf"});
            skLineSegment(sketch, "E215", {"start": v(-12.67, -86.91) * mm, "end": v(-12.67, -46.23) * mm, "construction": true});
            const initialGuessF19  = {"E214": [-0.0198, -0.08075, 1, 0, 0.01418]};
            skSetInitialGuess(sketch, initialGuessF19);
            skSolve(sketch);
        }
        {
            var Q0;
            Q0=qCreatedBy(makeId("Top.planeOp"),FACE);
            var sketch = newSketch(context, id + "F20", { "sketchPlane" : qUnion([Q0])});
            skLineSegment(sketch, "E216", {"start": v(1.45, -62.87) * mm, "end": v(21.45, -62.87) * mm});
            skLineSegment(sketch, "E217", {"start": v(21.45, -62.87) * mm, "end": v(21.45, -82.87) * mm});
            skLineSegment(sketch, "E218", {"start": v(21.45, -82.87) * mm, "end": v(11.45, -92.87) * mm});
            skPoint(sketch, "E218.endSnap0", {"position": v(11.45, -62.87) * mm});
            skLineSegment(sketch, "E219", {"start": v(11.45, -92.87) * mm, "end": v(1.45, -82.87) * mm});
            skLineSegment(sketch, "E220", {"start": v(1.45, -82.87) * mm, "end": v(1.45, -62.87) * mm});
            skLineSegment(sketch, "E221", {"start": v(3.85, -67.67) * mm, "end": v(19.05, -67.67) * mm});
            skLineSegment(sketch, "E222", {"start": v(19.05, -67.67) * mm, "end": v(19.05, -81.88) * mm});
            skLineSegment(sketch, "E223", {"start": v(19.05, -81.88) * mm, "end": v(11.45, -89.48) * mm});
            skLineSegment(sketch, "E224", {"start": v(11.45, -89.48) * mm, "end": v(3.85, -81.88) * mm});
            skLineSegment(sketch, "E225", {"start": v(3.85, -81.88) * mm, "end": v(3.85, -67.67) * mm});
            skText(sketch, "E226", { "text": "S", "fontName": "OpenSans-Bold.ttf"});
            skLineSegment(sketch, "E227", {"start": v(11.45, -80.26) * mm, "end": v(11.45, -52.69) * mm, "construction": true});
            const initialGuessF20  = {"E226": [0.00571, -0.08056, 1, 0, 0.01408]};
            skSetInitialGuess(sketch, initialGuessF20);
            skSolve(sketch);
        }
        {
            var Q0;
            Q0=qCreatedBy(makeId("Top.planeOp"),FACE);
            var sketch = newSketch(context, id + "F21", { "sketchPlane" : qUnion([Q0])});
            skLineSegment(sketch, "E228", {"start": v(24.93, -62.91) * mm, "end": v(44.93, -62.91) * mm});
            skLineSegment(sketch, "E229", {"start": v(44.93, -62.91) * mm, "end": v(44.93, -82.91) * mm});
            skLineSegment(sketch, "E230", {"start": v(44.93, -82.91) * mm, "end": v(34.93, -92.91) * mm});
            skPoint(sketch, "E230.endSnap0", {"position": v(34.93, -62.91) * mm});
            skLineSegment(sketch, "E231", {"start": v(34.93, -92.91) * mm, "end": v(24.93, -82.91) * mm});
            skLineSegment(sketch, "E232", {"start": v(24.93, -82.91) * mm, "end": v(24.93, -62.91) * mm});
            skLineSegment(sketch, "E233", {"start": v(27.33, -67.71) * mm, "end": v(42.53, -67.71) * mm});
            skLineSegment(sketch, "E234", {"start": v(42.53, -67.71) * mm, "end": v(42.53, -81.92) * mm});
            skLineSegment(sketch, "E235", {"start": v(42.53, -81.92) * mm, "end": v(34.93, -89.52) * mm});
            skLineSegment(sketch, "E236", {"start": v(34.93, -89.52) * mm, "end": v(27.33, -81.92) * mm});
            skLineSegment(sketch, "E237", {"start": v(27.33, -81.92) * mm, "end": v(27.33, -67.71) * mm});
            skText(sketch, "E238", { "text": "T", "fontName": "OpenSans-Bold.ttf"});
            skLineSegment(sketch, "E239", {"start": v(34.93, -84.52) * mm, "end": v(34.93, -48.5) * mm, "construction": true});
            const initialGuessF21  = {"E238": [0.02918, -0.08068, 1, 0, 0.01417]};
            skSetInitialGuess(sketch, initialGuessF21);
            skSolve(sketch);
        }
        {
            var Q0;
            Q0=qCreatedBy(makeId("Top.planeOp"),FACE);
            var sketch = newSketch(context, id + "F22", { "sketchPlane" : qUnion([Q0])});
            skLineSegment(sketch, "E240", {"start": v(-68.8, -97.37) * mm, "end": v(-48.8, -97.37) * mm});
            skLineSegment(sketch, "E241", {"start": v(-48.8, -97.37) * mm, "end": v(-48.8, -117.37) * mm});
            skLineSegment(sketch, "E242", {"start": v(-48.8, -117.37) * mm, "end": v(-58.8, -127.37) * mm});
            skPoint(sketch, "E242.endSnap0", {"position": v(-58.8, -97.37) * mm});
            skLineSegment(sketch, "E243", {"start": v(-58.8, -127.37) * mm, "end": v(-68.8, -117.37) * mm});
            skLineSegment(sketch, "E244", {"start": v(-68.8, -117.37) * mm, "end": v(-68.8, -97.37) * mm});
            skLineSegment(sketch, "E245", {"start": v(-66.4, -102.17) * mm, "end": v(-51.2, -102.17) * mm});
            skLineSegment(sketch, "E246", {"start": v(-51.2, -102.17) * mm, "end": v(-51.2, -116.38) * mm});
            skLineSegment(sketch, "E247", {"start": v(-51.2, -116.38) * mm, "end": v(-58.8, -123.98) * mm});
            skLineSegment(sketch, "E248", {"start": v(-58.8, -123.98) * mm, "end": v(-66.4, -116.38) * mm});
            skLineSegment(sketch, "E249", {"start": v(-66.4, -116.38) * mm, "end": v(-66.4, -102.17) * mm});
            skText(sketch, "E250", { "text": "U", "fontName": "OpenSans-Bold.ttf"});
            skLineSegment(sketch, "E251", {"start": v(-58.8, -114.48) * mm, "end": v(-58.8, -87.46) * mm, "construction": true});
            const initialGuessF22  = {"E250": [-0.06555, -0.11385, 1, 0, 0.01288]};
            skSetInitialGuess(sketch, initialGuessF22);
            skSolve(sketch);
        }
        {
            var Q0;
            Q0=qCreatedBy(makeId("Top.planeOp"),FACE);
            var sketch = newSketch(context, id + "F23", { "sketchPlane" : qUnion([Q0])});
            skLineSegment(sketch, "E252", {"start": v(-45.88, -97.28) * mm, "end": v(-25.88, -97.28) * mm});
            skLineSegment(sketch, "E253", {"start": v(-25.88, -97.28) * mm, "end": v(-25.88, -117.28) * mm});
            skLineSegment(sketch, "E254", {"start": v(-25.88, -117.28) * mm, "end": v(-35.88, -127.28) * mm});
            skPoint(sketch, "E254.endSnap0", {"position": v(-35.88, -97.28) * mm});
            skLineSegment(sketch, "E255", {"start": v(-35.88, -127.28) * mm, "end": v(-45.88, -117.28) * mm});
            skLineSegment(sketch, "E256", {"start": v(-45.88, -117.28) * mm, "end": v(-45.88, -97.28) * mm});
            skLineSegment(sketch, "E257", {"start": v(-43.48, -102.08) * mm, "end": v(-28.28, -102.08) * mm});
            skLineSegment(sketch, "E258", {"start": v(-28.28, -102.08) * mm, "end": v(-28.28, -116.29) * mm});
            skLineSegment(sketch, "E259", {"start": v(-28.28, -116.29) * mm, "end": v(-35.88, -123.89) * mm});
            skLineSegment(sketch, "E260", {"start": v(-35.88, -123.89) * mm, "end": v(-43.48, -116.29) * mm});
            skLineSegment(sketch, "E261", {"start": v(-43.48, -116.29) * mm, "end": v(-43.48, -102.08) * mm});
            skText(sketch, "E262", { "text": "V", "fontName": "OpenSans-Bold.ttf"});
            skLineSegment(sketch, "E263", {"start": v(-35.88, -119.45) * mm, "end": v(-35.88, -82.32) * mm, "construction": true});
            const initialGuessF23  = {"E262": [-0.0424, -0.11529, 1, 0, 0.0144]};
            skSetInitialGuess(sketch, initialGuessF23);
            skSolve(sketch);
        }
        {
            var Q0;
            Q0=qCreatedBy(makeId("Top.planeOp"),FACE);
            var sketch = newSketch(context, id + "F24", { "sketchPlane" : qUnion([Q0])});
            skLineSegment(sketch, "E264", {"start": v(-22.63, -97.13) * mm, "end": v(-2.63, -97.13) * mm});
            skLineSegment(sketch, "E265", {"start": v(-2.63, -97.13) * mm, "end": v(-2.63, -117.13) * mm});
            skLineSegment(sketch, "E266", {"start": v(-2.63, -117.13) * mm, "end": v(-12.63, -127.13) * mm});
            skPoint(sketch, "E266.endSnap0", {"position": v(-12.63, -97.13) * mm});
            skLineSegment(sketch, "E267", {"start": v(-12.63, -127.13) * mm, "end": v(-22.63, -117.13) * mm});
            skLineSegment(sketch, "E268", {"start": v(-22.63, -117.13) * mm, "end": v(-22.63, -97.13) * mm});
            skLineSegment(sketch, "E269", {"start": v(-20.23, -101.93) * mm, "end": v(-5.03, -101.93) * mm});
            skLineSegment(sketch, "E270", {"start": v(-5.03, -101.93) * mm, "end": v(-5.03, -116.14) * mm});
            skLineSegment(sketch, "E271", {"start": v(-5.03, -116.14) * mm, "end": v(-12.63, -123.74) * mm});
            skLineSegment(sketch, "E272", {"start": v(-12.63, -123.74) * mm, "end": v(-20.23, -116.14) * mm});
            skLineSegment(sketch, "E273", {"start": v(-20.23, -116.14) * mm, "end": v(-20.23, -101.93) * mm});
            skText(sketch, "E274", { "text": "W", "fontName": "OpenSans-Bold.ttf"});
            skLineSegment(sketch, "E275", {"start": v(-12.63, -120.83) * mm, "end": v(-12.63, -80.64) * mm, "construction": true});
            const initialGuessF24  = {"E274": [-0.02065, -0.11265, 1, 0, 0.01191]};
            skSetInitialGuess(sketch, initialGuessF24);
            skSolve(sketch);
        }
        {
            var Q0;
            Q0=qCreatedBy(makeId("Top.planeOp"),FACE);
            var sketch = newSketch(context, id + "F25", { "sketchPlane" : qUnion([Q0])});
            skLineSegment(sketch, "E276", {"start": v(1.44, -97.2) * mm, "end": v(21.44, -97.2) * mm});
            skLineSegment(sketch, "E277", {"start": v(21.44, -97.2) * mm, "end": v(21.44, -117.2) * mm});
            skLineSegment(sketch, "E278", {"start": v(21.44, -117.2) * mm, "end": v(11.44, -127.2) * mm});
            skPoint(sketch, "E278.endSnap0", {"position": v(11.44, -97.2) * mm});
            skLineSegment(sketch, "E279", {"start": v(11.44, -127.2) * mm, "end": v(1.44, -117.2) * mm});
            skLineSegment(sketch, "E280", {"start": v(1.44, -117.2) * mm, "end": v(1.44, -97.2) * mm});
            skLineSegment(sketch, "E281", {"start": v(3.84, -102) * mm, "end": v(19.04, -102) * mm});
            skLineSegment(sketch, "E282", {"start": v(19.04, -102) * mm, "end": v(19.04, -116.21) * mm});
            skLineSegment(sketch, "E283", {"start": v(19.04, -116.21) * mm, "end": v(11.44, -123.81) * mm});
            skLineSegment(sketch, "E284", {"start": v(11.44, -123.81) * mm, "end": v(3.84, -116.21) * mm});
            skLineSegment(sketch, "E285", {"start": v(3.84, -116.21) * mm, "end": v(3.84, -102) * mm});
            skText(sketch, "E286", { "text": "X", "fontName": "OpenSans-Bold.ttf"});
            skLineSegment(sketch, "E287", {"start": v(11.44, -120.38) * mm, "end": v(11.44, -81.24) * mm, "construction": true});
            const initialGuessF25  = {"E286": [0.00472, -0.11484, 1, 0, 0.01403]};
            skSetInitialGuess(sketch, initialGuessF25);
            skSolve(sketch);
        }
        {
            var Q0;
            Q0=qCreatedBy(makeId("Top.planeOp"),FACE);
            var sketch = newSketch(context, id + "F26", { "sketchPlane" : qUnion([Q0])});
            skLineSegment(sketch, "E288", {"start": v(24.9, -97.05) * mm, "end": v(44.9, -97.05) * mm});
            skLineSegment(sketch, "E289", {"start": v(44.9, -97.05) * mm, "end": v(44.9, -117.05) * mm});
            skLineSegment(sketch, "E290", {"start": v(44.9, -117.05) * mm, "end": v(34.9, -127.05) * mm});
            skPoint(sketch, "E290.endSnap0", {"position": v(34.9, -97.05) * mm});
            skLineSegment(sketch, "E291", {"start": v(34.9, -127.05) * mm, "end": v(24.9, -117.05) * mm});
            skLineSegment(sketch, "E292", {"start": v(24.9, -117.05) * mm, "end": v(24.9, -97.05) * mm});
            skLineSegment(sketch, "E293", {"start": v(27.3, -101.85) * mm, "end": v(42.5, -101.85) * mm});
            skLineSegment(sketch, "E294", {"start": v(42.5, -101.85) * mm, "end": v(42.5, -116.05) * mm});
            skLineSegment(sketch, "E295", {"start": v(42.5, -116.05) * mm, "end": v(34.9, -123.65) * mm});
            skLineSegment(sketch, "E296", {"start": v(34.9, -123.65) * mm, "end": v(27.3, -116.05) * mm});
            skLineSegment(sketch, "E297", {"start": v(27.3, -116.05) * mm, "end": v(27.3, -101.85) * mm});
            skText(sketch, "E298", { "text": "Y", "fontName": "OpenSans-Bold.ttf"});
            skLineSegment(sketch, "E299", {"start": v(34.9, -120.82) * mm, "end": v(34.9, -80.48) * mm, "construction": true});
            const initialGuessF26  = {"E298": [0.02843, -0.11565, 1, 0, 0.015]};
            skSetInitialGuess(sketch, initialGuessF26);
            skSolve(sketch);
        }
        {
            var Q0;
            Q0=qCreatedBy(makeId("Top.planeOp"),FACE);
            var sketch = newSketch(context, id + "F27", { "sketchPlane" : qUnion([Q0])});
            skLineSegment(sketch, "E300", {"start": v(49.07, -29.8) * mm, "end": v(69.07, -29.8) * mm});
            skLineSegment(sketch, "E301", {"start": v(69.07, -29.8) * mm, "end": v(69.07, -49.8) * mm});
            skLineSegment(sketch, "E302", {"start": v(69.07, -49.8) * mm, "end": v(59.07, -59.8) * mm});
            skPoint(sketch, "E302.endSnap0", {"position": v(59.07, -29.8) * mm});
            skLineSegment(sketch, "E303", {"start": v(59.07, -59.8) * mm, "end": v(49.07, -49.8) * mm});
            skLineSegment(sketch, "E304", {"start": v(49.07, -49.8) * mm, "end": v(49.07, -29.8) * mm});
            skLineSegment(sketch, "E305", {"start": v(51.47, -34.6) * mm, "end": v(66.67, -34.6) * mm});
            skLineSegment(sketch, "E306", {"start": v(66.67, -34.6) * mm, "end": v(66.67, -48.81) * mm});
            skLineSegment(sketch, "E307", {"start": v(66.67, -48.81) * mm, "end": v(59.07, -56.41) * mm});
            skLineSegment(sketch, "E308", {"start": v(59.07, -56.41) * mm, "end": v(51.47, -48.81) * mm});
            skLineSegment(sketch, "E309", {"start": v(51.47, -48.81) * mm, "end": v(51.47, -34.6) * mm});
            skText(sketch, "E310", { "text": "Z", "fontName": "OpenSans-Bold.ttf"});
            skLineSegment(sketch, "E311", {"start": v(59.07, -53.8) * mm, "end": v(59.07, -13) * mm, "construction": true});
            const initialGuessF27  = {"E310": [0.05323, -0.04767, 1, 0, 0.01427]};
            skSetInitialGuess(sketch, initialGuessF27);
            skSolve(sketch);
        }
        {
            var Q0;
            {var subQ5=sQuery(id+"F2.wireOp",EDGE,"E10.sketch_text.stroke-5");Q0=makeQuery(id+"F2.imprint","IMPRINT",FACE,{"disambiguationData":[TD([[makeQuery(id+"F2.imprint","IMPRINT",EDGE,{"derivedFrom":subQ5}),-1.0]])]});}
            var Q1;
            Q1=makeQuery(id+"F2.imprint","IMPRINT",FACE,{"disambiguationData":[TD([[makeQuery(id+"F2.imprint","IMPRINT",EDGE,{"derivedFrom":sQuery(id+"F2.wireOp",EDGE,"E10.sketch_text.stroke-0")}),-1.0]])]});
            var Q2;
            {var subQ2=sQuery(id+"F3.wireOp",EDGE,"E22.sketch_text.stroke-0");Q2=makeQuery(id+"F3.imprint","IMPRINT",FACE,{"disambiguationData":[TD([[makeQuery(id+"F3.imprint","IMPRINT",EDGE,{"derivedFrom":subQ2}),-1.0]])]});}
            var Q3;
            {var subQ4=sQuery(id+"F3.wireOp",EDGE,"E22.sketch_text.stroke-3");Q3=makeQuery(id+"F3.imprint","IMPRINT",FACE,{"disambiguationData":[TD([[makeQuery(id+"F3.imprint","IMPRINT",EDGE,{"derivedFrom":subQ4}),-1.0]])]});}
            var Q4;
            {var subQ1=sQuery(id+"F4.wireOp",EDGE,"E34.sketch_text.stroke-10");Q4=makeQuery(id+"F4.imprint","IMPRINT",FACE,{"disambiguationData":[TD([[makeQuery(id+"F4.imprint","IMPRINT",EDGE,{"derivedFrom":subQ1}),-1.0]])]});}
            var Q5;
            Q5=makeQuery(id+"F4.imprint","IMPRINT",FACE,{"disambiguationData":[TD([[makeQuery(id+"F4.imprint","IMPRINT",EDGE,{"derivedFrom":sQuery(id+"F4.wireOp",EDGE,"E34.sketch_text.stroke-0")}),-1.0]])]});
            var Q6;
            {var subQ5=sQuery(id+"F5.wireOp",EDGE,"E46.sketch_text.stroke-4");Q6=makeQuery(id+"F5.imprint","IMPRINT",FACE,{"disambiguationData":[TD([[makeQuery(id+"F5.imprint","IMPRINT",EDGE,{"derivedFrom":subQ5}),-1.0]])]});}
            var Q7;
            Q7=makeQuery(id+"F5.imprint","IMPRINT",FACE,{"disambiguationData":[TD([[makeQuery(id+"F5.imprint","IMPRINT",EDGE,{"derivedFrom":sQuery(id+"F5.wireOp",EDGE,"E46.sketch_text.stroke-0")}),-1.0]])]});
            var Q8;
            {var subQ5=sQuery(id+"F6.wireOp",EDGE,"E58.sketch_text.stroke-2");Q8=makeQuery(id+"F6.imprint","IMPRINT",FACE,{"disambiguationData":[TD([[makeQuery(id+"F6.imprint","IMPRINT",EDGE,{"derivedFrom":subQ5}),-1.0]])]});}
            var Q9;
            {var subQ1=sQuery(id+"F6.wireOp",EDGE,"E58.sketch_text.stroke-0");Q9=makeQuery(id+"F6.imprint","IMPRINT",FACE,{"disambiguationData":[TD([[makeQuery(id+"F6.imprint","IMPRINT",EDGE,{"derivedFrom":subQ1}),-1.0]])]});}
            var Q10;
            {var subQ5=sQuery(id+"F7.wireOp",EDGE,"E70.sketch_text.stroke-2");Q10=makeQuery(id+"F7.imprint","IMPRINT",FACE,{"disambiguationData":[TD([[makeQuery(id+"F7.imprint","IMPRINT",EDGE,{"derivedFrom":subQ5}),-1.0]])]});}
            var Q11;
            {var subQ5=sQuery(id+"F7.wireOp",EDGE,"E70.sketch_text.stroke-0");Q11=makeQuery(id+"F7.imprint","IMPRINT",FACE,{"disambiguationData":[TD([[makeQuery(id+"F7.imprint","IMPRINT",EDGE,{"derivedFrom":subQ5}),-1.0]])]});}
            var Q12;
            {var subQ5=sQuery(id+"F8.wireOp",EDGE,"E82.sketch_text.stroke-8");Q12=makeQuery(id+"F8.imprint","IMPRINT",FACE,{"disambiguationData":[TD([[makeQuery(id+"F8.imprint","IMPRINT",EDGE,{"derivedFrom":subQ5}),-1.0]])]});}
            var Q13;
            Q13=makeQuery(id+"F8.imprint","IMPRINT",FACE,{"disambiguationData":[TD([[makeQuery(id+"F8.imprint","IMPRINT",EDGE,{"derivedFrom":sQuery(id+"F8.wireOp",EDGE,"E82.sketch_text.stroke-0")}),-1.0]])]});
            var Q14;
            {var subQ5=sQuery(id+"F9.wireOp",EDGE,"E94.sketch_text.stroke-6");Q14=makeQuery(id+"F9.imprint","IMPRINT",FACE,{"disambiguationData":[TD([[makeQuery(id+"F9.imprint","IMPRINT",EDGE,{"derivedFrom":subQ5}),-1.0]])]});}
            var Q15;
            {var subQ5=sQuery(id+"F9.wireOp",EDGE,"E94.sketch_text.stroke-10");Q15=makeQuery(id+"F9.imprint","IMPRINT",FACE,{"disambiguationData":[TD([[makeQuery(id+"F9.imprint","IMPRINT",EDGE,{"derivedFrom":subQ5}),-1.0]])]});}
            var Q16;
            {var subQ9=sQuery(id+"F9.wireOp",EDGE,"E94.sketch_text.stroke-0");Q16=makeQuery(id+"F9.imprint","IMPRINT",FACE,{"disambiguationData":[TD([[makeQuery(id+"F9.imprint","IMPRINT",EDGE,{"derivedFrom":subQ9}),-1.0]])]});}
            var Q17;
            {var subQ5=sQuery(id+"F10.wireOp",EDGE,"E106.sketch_text.stroke-1");Q17=makeQuery(id+"F10.imprint","IMPRINT",FACE,{"disambiguationData":[TD([[makeQuery(id+"F10.imprint","IMPRINT",EDGE,{"derivedFrom":subQ5}),-1.0]])]});}
            var Q18;
            {var subQ5=sQuery(id+"F10.wireOp",EDGE,"E106.sketch_text.stroke-3");Q18=makeQuery(id+"F10.imprint","IMPRINT",FACE,{"disambiguationData":[TD([[makeQuery(id+"F10.imprint","IMPRINT",EDGE,{"derivedFrom":subQ5}),-1.0]])]});}
            var Q19;
            {var subQ5=sQuery(id+"F11.wireOp",EDGE,"E118.sketch_text.stroke-6");Q19=makeQuery(id+"F11.imprint","IMPRINT",FACE,{"disambiguationData":[TD([[makeQuery(id+"F11.imprint","IMPRINT",EDGE,{"derivedFrom":subQ5}),-1.0]])]});}
            var Q20;
            Q20=makeQuery(id+"F11.imprint","IMPRINT",FACE,{"disambiguationData":[TD([[makeQuery(id+"F11.imprint","IMPRINT",EDGE,{"derivedFrom":sQuery(id+"F11.wireOp",EDGE,"E118.sketch_text.stroke-0")}),-1.0]])]});
            var Q21;
            {var subQ5=sQuery(id+"F12.wireOp",EDGE,"E130.sketch_text.stroke-6");Q21=makeQuery(id+"F12.imprint","IMPRINT",FACE,{"disambiguationData":[TD([[makeQuery(id+"F12.imprint","IMPRINT",EDGE,{"derivedFrom":subQ5}),-1.0]])]});}
            var Q22;
            {var subQ5=sQuery(id+"F12.wireOp",EDGE,"E130.sketch_text.stroke-10");Q22=makeQuery(id+"F12.imprint","IMPRINT",FACE,{"disambiguationData":[TD([[makeQuery(id+"F12.imprint","IMPRINT",EDGE,{"derivedFrom":subQ5}),-1.0]])]});}
            var Q23;
            Q23=makeQuery(id+"F12.imprint","IMPRINT",FACE,{"disambiguationData":[TD([[makeQuery(id+"F12.imprint","IMPRINT",EDGE,{"derivedFrom":sQuery(id+"F12.wireOp",EDGE,"E130.sketch_text.stroke-0")}),-1.0]])]});
            var Q24;
            {var subQ5=sQuery(id+"F13.wireOp",EDGE,"E142.sketch_text.stroke-1");Q24=makeQuery(id+"F13.imprint","IMPRINT",FACE,{"disambiguationData":[TD([[makeQuery(id+"F13.imprint","IMPRINT",EDGE,{"derivedFrom":subQ5}),-1.0]])]});}
            var Q25;
            {var subQ0=sQuery(id+"F13.wireOp",EDGE,"E142.sketch_text.stroke-3");Q25=makeQuery(id+"F13.imprint","IMPRINT",FACE,{"disambiguationData":[TD([[makeQuery(id+"F13.imprint","IMPRINT",EDGE,{"derivedFrom":subQ0}),-1.0]])]});}
            var Q26;
            {var subQ5=sQuery(id+"F14.wireOp",EDGE,"E154.sketch_text.stroke-6");Q26=makeQuery(id+"F14.imprint","IMPRINT",FACE,{"disambiguationData":[TD([[makeQuery(id+"F14.imprint","IMPRINT",EDGE,{"derivedFrom":subQ5}),-1.0]])]});}
            var Q27;
            {var subQ5=sQuery(id+"F14.wireOp",EDGE,"E154.sketch_text.stroke-10");Q27=makeQuery(id+"F14.imprint","IMPRINT",FACE,{"disambiguationData":[TD([[makeQuery(id+"F14.imprint","IMPRINT",EDGE,{"derivedFrom":subQ5}),-1.0]])]});}
            var Q28;
            Q28=makeQuery(id+"F14.imprint","IMPRINT",FACE,{"disambiguationData":[TD([[makeQuery(id+"F14.imprint","IMPRINT",EDGE,{"derivedFrom":sQuery(id+"F14.wireOp",EDGE,"E154.sketch_text.stroke-0")}),-1.0]])]});
            var Q29;
            {var subQ5=sQuery(id+"F15.wireOp",EDGE,"E166.sketch_text.stroke-7");Q29=makeQuery(id+"F15.imprint","IMPRINT",FACE,{"disambiguationData":[TD([[makeQuery(id+"F15.imprint","IMPRINT",EDGE,{"derivedFrom":subQ5}),-1.0]])]});}
            var Q30;
            {var subQ5=sQuery(id+"F15.wireOp",EDGE,"E166.sketch_text.stroke-12");Q30=makeQuery(id+"F15.imprint","IMPRINT",FACE,{"disambiguationData":[TD([[makeQuery(id+"F15.imprint","IMPRINT",EDGE,{"derivedFrom":subQ5}),-1.0]])]});}
            var Q31;
            {var subQ7=sQuery(id+"F15.wireOp",EDGE,"E166.sketch_text.stroke-0");Q31=makeQuery(id+"F15.imprint","IMPRINT",FACE,{"disambiguationData":[TD([[makeQuery(id+"F15.imprint","IMPRINT",EDGE,{"derivedFrom":subQ7}),-1.0]])]});}
            var Q32;
            {var subQ0=sQuery(id+"F16.wireOp",EDGE,"E178.sketch_text.stroke-5");var subQ1=sQuery(id+"F16.wireOp",EDGE,"E173");var subQ2=makeQuery(id+"F16.imprint","INTERSECT",VERTEX,{"derivedFrom":[subQ1,subQ0]});Q32=makeQuery(id+"F16.imprint","IMPRINT",FACE,{"disambiguationData":[TD([[makeQuery(id+"F16.imprint","IMPRINT",EDGE,{"disambiguationData":[TD([[subQ2,-1.0]])],"derivedFrom":subQ1}),1.0]])]});}
            var Q33;
            Q33=makeQuery(id+"F16.imprint","IMPRINT",FACE,{"disambiguationData":[TD([[makeQuery(id+"F16.imprint","IMPRINT",EDGE,{"derivedFrom":sQuery(id+"F16.wireOp",EDGE,"E178.sketch_text.stroke-0")}),-1.0]])]});
            var Q34;
            {var subQ5=sQuery(id+"F17.wireOp",EDGE,"E190.sketch_text.stroke-13");Q34=makeQuery(id+"F17.imprint","IMPRINT",FACE,{"disambiguationData":[TD([[makeQuery(id+"F17.imprint","IMPRINT",EDGE,{"derivedFrom":subQ5}),-1.0]])]});}
            var Q35;
            Q35=makeQuery(id+"F17.imprint","IMPRINT",FACE,{"disambiguationData":[TD([[makeQuery(id+"F17.imprint","IMPRINT",EDGE,{"derivedFrom":sQuery(id+"F17.wireOp",EDGE,"E190.sketch_text.stroke-0")}),-1.0]])]});
            var Q36;
            {var subQ0=sQuery(id+"F18.wireOp",EDGE,"E202.sketch_text.stroke-9");var subQ1=sQuery(id+"F18.wireOp",EDGE,"E197");var subQ2=makeQuery(id+"F18.imprint","INTERSECT",VERTEX,{"derivedFrom":[subQ1,subQ0]});Q36=makeQuery(id+"F18.imprint","IMPRINT",FACE,{"disambiguationData":[TD([[makeQuery(id+"F18.imprint","IMPRINT",EDGE,{"disambiguationData":[TD([[subQ2,-1.0]])],"derivedFrom":subQ1}),1.0]])]});}
            var Q37;
            Q37=makeQuery(id+"F18.imprint","IMPRINT",FACE,{"disambiguationData":[TD([[makeQuery(id+"F18.imprint","IMPRINT",EDGE,{"derivedFrom":sQuery(id+"F18.wireOp",EDGE,"E202.sketch_text.stroke-0")}),-1.0]])]});
            var Q38;
            {var subQ1=sQuery(id+"F19.wireOp",EDGE,"E214.sketch_text.stroke-10");Q38=makeQuery(id+"F19.imprint","IMPRINT",FACE,{"disambiguationData":[TD([[makeQuery(id+"F19.imprint","IMPRINT",EDGE,{"derivedFrom":subQ1}),-1.0]])]});}
            var Q39;
            Q39=makeQuery(id+"F19.imprint","IMPRINT",FACE,{"disambiguationData":[TD([[makeQuery(id+"F19.imprint","IMPRINT",EDGE,{"derivedFrom":sQuery(id+"F19.wireOp",EDGE,"E214.sketch_text.stroke-0")}),-1.0]])]});
            var Q40;
            {var subQ0=sQuery(id+"F20.wireOp",EDGE,"E226.sketch_text.stroke-15");Q40=makeQuery(id+"F20.imprint","IMPRINT",FACE,{"disambiguationData":[TD([[makeQuery(id+"F20.imprint","IMPRINT",EDGE,{"derivedFrom":subQ0}),-1.0]])]});}
            var Q41;
            Q41=makeQuery(id+"F20.imprint","IMPRINT",FACE,{"disambiguationData":[TD([[makeQuery(id+"F20.imprint","IMPRINT",EDGE,{"derivedFrom":sQuery(id+"F20.wireOp",EDGE,"E226.sketch_text.stroke-0")}),-1.0]])]});
            var Q42;
            {var subQ5=sQuery(id+"F21.wireOp",EDGE,"E238.sketch_text.stroke-4");Q42=makeQuery(id+"F21.imprint","IMPRINT",FACE,{"disambiguationData":[TD([[makeQuery(id+"F21.imprint","IMPRINT",EDGE,{"derivedFrom":subQ5}),-1.0]])]});}
            var Q43;
            Q43=makeQuery(id+"F21.imprint","IMPRINT",FACE,{"disambiguationData":[TD([[makeQuery(id+"F21.imprint","IMPRINT",EDGE,{"derivedFrom":sQuery(id+"F21.wireOp",EDGE,"E238.sketch_text.stroke-0")}),-1.0]])]});
            var Q44;
            {var subQ5=sQuery(id+"F22.wireOp",EDGE,"E250.sketch_text.stroke-7");Q44=makeQuery(id+"F22.imprint","IMPRINT",FACE,{"disambiguationData":[TD([[makeQuery(id+"F22.imprint","IMPRINT",EDGE,{"derivedFrom":subQ5}),-1.0]])]});}
            var Q45;
            {var subQ5=sQuery(id+"F22.wireOp",EDGE,"E250.sketch_text.stroke-14");Q45=makeQuery(id+"F22.imprint","IMPRINT",FACE,{"disambiguationData":[TD([[makeQuery(id+"F22.imprint","IMPRINT",EDGE,{"derivedFrom":subQ5}),-1.0]])]});}
            var Q46;
            {var subQ10=sQuery(id+"F22.wireOp",EDGE,"E250.sketch_text.stroke-1");Q46=makeQuery(id+"F22.imprint","IMPRINT",FACE,{"disambiguationData":[TD([[makeQuery(id+"F22.imprint","IMPRINT",EDGE,{"derivedFrom":subQ10}),-1.0]])]});}
            var Q47;
            {var subQ5=sQuery(id+"F23.wireOp",EDGE,"E262.sketch_text.stroke-4");Q47=makeQuery(id+"F23.imprint","IMPRINT",FACE,{"disambiguationData":[TD([[makeQuery(id+"F23.imprint","IMPRINT",EDGE,{"derivedFrom":subQ5}),-1.0]])]});}
            var Q48;
            {var subQ0=sQuery(id+"F23.wireOp",EDGE,"E262.sketch_text.stroke-2");Q48=makeQuery(id+"F23.imprint","IMPRINT",FACE,{"disambiguationData":[TD([[makeQuery(id+"F23.imprint","IMPRINT",EDGE,{"derivedFrom":subQ0}),-1.0]])]});}
            var Q49;
            {var subQ5=sQuery(id+"F23.wireOp",EDGE,"E262.sketch_text.stroke-0");Q49=makeQuery(id+"F23.imprint","IMPRINT",FACE,{"disambiguationData":[TD([[makeQuery(id+"F23.imprint","IMPRINT",EDGE,{"derivedFrom":subQ5}),-1.0]])]});}
            var Q50;
            {var subQ0=sQuery(id+"F24.wireOp",EDGE,"E274.sketch_text.stroke-9");Q50=makeQuery(id+"F24.imprint","IMPRINT",FACE,{"disambiguationData":[TD([[makeQuery(id+"F24.imprint","IMPRINT",EDGE,{"derivedFrom":subQ0}),-1.0]])]});}
            var Q51;
            {var subQ14=sQuery(id+"F24.wireOp",EDGE,"E274.sketch_text.stroke-0");Q51=makeQuery(id+"F24.imprint","IMPRINT",FACE,{"disambiguationData":[TD([[makeQuery(id+"F24.imprint","IMPRINT",EDGE,{"derivedFrom":subQ14}),-1.0]])]});}
            var Q52;
            {var subQ5=sQuery(id+"F24.wireOp",EDGE,"E274.sketch_text.stroke-15");Q52=makeQuery(id+"F24.imprint","IMPRINT",FACE,{"disambiguationData":[TD([[makeQuery(id+"F24.imprint","IMPRINT",EDGE,{"derivedFrom":subQ5}),-1.0]])]});}
            var Q53;
            {var subQ0=sQuery(id+"F24.wireOp",EDGE,"E274.sketch_text.stroke-22");Q53=makeQuery(id+"F24.imprint","IMPRINT",FACE,{"disambiguationData":[TD([[makeQuery(id+"F24.imprint","IMPRINT",EDGE,{"derivedFrom":subQ0}),-1.0]])]});}
            var Q54;
            {var subQ5=sQuery(id+"F25.wireOp",EDGE,"E286.sketch_text.stroke-6");Q54=makeQuery(id+"F25.imprint","IMPRINT",FACE,{"disambiguationData":[TD([[makeQuery(id+"F25.imprint","IMPRINT",EDGE,{"derivedFrom":subQ5}),-1.0]])]});}
            var Q55;
            Q55=makeQuery(id+"F25.imprint","IMPRINT",FACE,{"disambiguationData":[TD([[makeQuery(id+"F25.imprint","IMPRINT",EDGE,{"derivedFrom":sQuery(id+"F25.wireOp",EDGE,"E286.sketch_text.stroke-0")}),-1.0]])]});
            var Q56;
            {var subQ5=sQuery(id+"F25.wireOp",EDGE,"E286.sketch_text.stroke-9");Q56=makeQuery(id+"F25.imprint","IMPRINT",FACE,{"disambiguationData":[TD([[makeQuery(id+"F25.imprint","IMPRINT",EDGE,{"derivedFrom":subQ5}),-1.0]])]});}
            var Q57;
            {var subQ5=sQuery(id+"F26.wireOp",EDGE,"E298.sketch_text.stroke-7");Q57=makeQuery(id+"F26.imprint","IMPRINT",FACE,{"disambiguationData":[TD([[makeQuery(id+"F26.imprint","IMPRINT",EDGE,{"derivedFrom":subQ5}),-1.0]])]});}
            var Q58;
            {var subQ5=sQuery(id+"F26.wireOp",EDGE,"E298.sketch_text.stroke-1");Q58=makeQuery(id+"F26.imprint","IMPRINT",FACE,{"disambiguationData":[TD([[makeQuery(id+"F26.imprint","IMPRINT",EDGE,{"derivedFrom":subQ5}),-1.0]])]});}
            var Q59;
            {var subQ0=sQuery(id+"F26.wireOp",EDGE,"E298.sketch_text.stroke-3");Q59=makeQuery(id+"F26.imprint","IMPRINT",FACE,{"disambiguationData":[TD([[makeQuery(id+"F26.imprint","IMPRINT",EDGE,{"derivedFrom":subQ0}),-1.0]])]});}
            var Q60;
            {var subQ5=sQuery(id+"F27.wireOp",EDGE,"E310.sketch_text.stroke-5");Q60=makeQuery(id+"F27.imprint","IMPRINT",FACE,{"disambiguationData":[TD([[makeQuery(id+"F27.imprint","IMPRINT",EDGE,{"derivedFrom":subQ5}),-1.0]])]});}
            var Q61;
            Q61=makeQuery(id+"F27.imprint","IMPRINT",FACE,{"disambiguationData":[TD([[makeQuery(id+"F27.imprint","IMPRINT",EDGE,{"derivedFrom":sQuery(id+"F27.wireOp",EDGE,"E310.sketch_text.stroke-0")}),-1.0]])]});
            extrude(context, id + "F28", {"entities" : qUnion([Q0, Q1, Q2, Q3, Q4, Q5, Q6, Q7, Q8, Q9, Q10, Q11, Q12, Q13, Q14, Q15, Q16, Q17, Q18, Q19, Q20, Q21, Q22, Q23, Q24, Q25, Q26, Q27, Q28, Q29, Q30, Q31, Q32, Q33, Q34, Q35, Q36, Q37, Q38, Q39, Q40, Q41, Q42, Q43, Q44, Q45, Q46, Q47, Q48, Q49, Q50, Q51, Q52, Q53, Q54, Q55, Q56, Q57, Q58, Q59, Q60, Q61]), "depth" : (getVariable(context, 'LetterWidth')) * mm});
        }
        {
            var Q0;
            Q0=makeQuery(id+"F2.imprint","IMPRINT",FACE,{"disambiguationData":[TD([[makeQuery(id+"F2.imprint","IMPRINT",EDGE,{"derivedFrom":sQuery(id+"F2.wireOp",EDGE,"E0")}),-1.0]])]});
            var Q1;
            Q1=makeQuery(id+"F3.imprint","IMPRINT",FACE,{"disambiguationData":[TD([[makeQuery(id+"F3.imprint","IMPRINT",EDGE,{"derivedFrom":sQuery(id+"F3.wireOp",EDGE,"E12")}),-1.0]])]});
            var Q2;
            Q2=makeQuery(id+"F4.imprint","IMPRINT",FACE,{"disambiguationData":[TD([[makeQuery(id+"F4.imprint","IMPRINT",EDGE,{"derivedFrom":sQuery(id+"F4.wireOp",EDGE,"E24")}),-1.0]])]});
            var Q3;
            Q3=makeQuery(id+"F5.imprint","IMPRINT",FACE,{"disambiguationData":[TD([[makeQuery(id+"F5.imprint","IMPRINT",EDGE,{"derivedFrom":sQuery(id+"F5.wireOp",EDGE,"E36")}),-1.0]])]});
            var Q4;
            Q4=makeQuery(id+"F6.imprint","IMPRINT",FACE,{"disambiguationData":[TD([[makeQuery(id+"F6.imprint","IMPRINT",EDGE,{"derivedFrom":sQuery(id+"F6.wireOp",EDGE,"E48")}),-1.0]])]});
            var Q5;
            Q5=makeQuery(id+"F7.imprint","IMPRINT",FACE,{"disambiguationData":[TD([[makeQuery(id+"F7.imprint","IMPRINT",EDGE,{"derivedFrom":sQuery(id+"F7.wireOp",EDGE,"E60")}),-1.0]])]});
            var Q6;
            Q6=makeQuery(id+"F8.imprint","IMPRINT",FACE,{"disambiguationData":[TD([[makeQuery(id+"F8.imprint","IMPRINT",EDGE,{"derivedFrom":sQuery(id+"F8.wireOp",EDGE,"E72")}),-1.0]])]});
            var Q7;
            Q7=makeQuery(id+"F9.imprint","IMPRINT",FACE,{"disambiguationData":[TD([[makeQuery(id+"F9.imprint","IMPRINT",EDGE,{"derivedFrom":sQuery(id+"F9.wireOp",EDGE,"E84")}),-1.0]])]});
            var Q8;
            Q8=makeQuery(id+"F10.imprint","IMPRINT",FACE,{"disambiguationData":[TD([[makeQuery(id+"F10.imprint","IMPRINT",EDGE,{"derivedFrom":sQuery(id+"F10.wireOp",EDGE,"E96")}),-1.0]])]});
            var Q9;
            Q9=makeQuery(id+"F11.imprint","IMPRINT",FACE,{"disambiguationData":[TD([[makeQuery(id+"F11.imprint","IMPRINT",EDGE,{"derivedFrom":sQuery(id+"F11.wireOp",EDGE,"E108")}),-1.0]])]});
            var Q10;
            Q10=makeQuery(id+"F12.imprint","IMPRINT",FACE,{"disambiguationData":[TD([[makeQuery(id+"F12.imprint","IMPRINT",EDGE,{"derivedFrom":sQuery(id+"F12.wireOp",EDGE,"E120")}),-1.0]])]});
            var Q11;
            Q11=makeQuery(id+"F13.imprint","IMPRINT",FACE,{"disambiguationData":[TD([[makeQuery(id+"F13.imprint","IMPRINT",EDGE,{"derivedFrom":sQuery(id+"F13.wireOp",EDGE,"E132")}),-1.0]])]});
            var Q12;
            Q12=makeQuery(id+"F14.imprint","IMPRINT",FACE,{"disambiguationData":[TD([[makeQuery(id+"F14.imprint","IMPRINT",EDGE,{"derivedFrom":sQuery(id+"F14.wireOp",EDGE,"E144")}),-1.0]])]});
            var Q13;
            Q13=makeQuery(id+"F15.imprint","IMPRINT",FACE,{"disambiguationData":[TD([[makeQuery(id+"F15.imprint","IMPRINT",EDGE,{"derivedFrom":sQuery(id+"F15.wireOp",EDGE,"E156")}),-1.0]])]});
            var Q14;
            Q14=makeQuery(id+"F16.imprint","IMPRINT",FACE,{"disambiguationData":[TD([[makeQuery(id+"F16.imprint","IMPRINT",EDGE,{"derivedFrom":sQuery(id+"F16.wireOp",EDGE,"E168")}),-1.0]])]});
            var Q15;
            Q15=makeQuery(id+"F17.imprint","IMPRINT",FACE,{"disambiguationData":[TD([[makeQuery(id+"F17.imprint","IMPRINT",EDGE,{"derivedFrom":sQuery(id+"F17.wireOp",EDGE,"E180")}),-1.0]])]});
            var Q16;
            Q16=makeQuery(id+"F18.imprint","IMPRINT",FACE,{"disambiguationData":[TD([[makeQuery(id+"F18.imprint","IMPRINT",EDGE,{"derivedFrom":sQuery(id+"F18.wireOp",EDGE,"E192")}),-1.0]])]});
            var Q17;
            Q17=makeQuery(id+"F19.imprint","IMPRINT",FACE,{"disambiguationData":[TD([[makeQuery(id+"F19.imprint","IMPRINT",EDGE,{"derivedFrom":sQuery(id+"F19.wireOp",EDGE,"E204")}),-1.0]])]});
            var Q18;
            Q18=makeQuery(id+"F20.imprint","IMPRINT",FACE,{"disambiguationData":[TD([[makeQuery(id+"F20.imprint","IMPRINT",EDGE,{"derivedFrom":sQuery(id+"F20.wireOp",EDGE,"E216")}),-1.0]])]});
            var Q19;
            Q19=makeQuery(id+"F21.imprint","IMPRINT",FACE,{"disambiguationData":[TD([[makeQuery(id+"F21.imprint","IMPRINT",EDGE,{"derivedFrom":sQuery(id+"F21.wireOp",EDGE,"E228")}),-1.0]])]});
            var Q20;
            Q20=makeQuery(id+"F22.imprint","IMPRINT",FACE,{"disambiguationData":[TD([[makeQuery(id+"F22.imprint","IMPRINT",EDGE,{"derivedFrom":sQuery(id+"F22.wireOp",EDGE,"E240")}),-1.0]])]});
            var Q21;
            Q21=makeQuery(id+"F23.imprint","IMPRINT",FACE,{"disambiguationData":[TD([[makeQuery(id+"F23.imprint","IMPRINT",EDGE,{"derivedFrom":sQuery(id+"F23.wireOp",EDGE,"E252")}),-1.0]])]});
            var Q22;
            Q22=makeQuery(id+"F24.imprint","IMPRINT",FACE,{"disambiguationData":[TD([[makeQuery(id+"F24.imprint","IMPRINT",EDGE,{"derivedFrom":sQuery(id+"F24.wireOp",EDGE,"E264")}),-1.0]])]});
            var Q23;
            Q23=makeQuery(id+"F25.imprint","IMPRINT",FACE,{"disambiguationData":[TD([[makeQuery(id+"F25.imprint","IMPRINT",EDGE,{"derivedFrom":sQuery(id+"F25.wireOp",EDGE,"E276")}),-1.0]])]});
            var Q24;
            Q24=makeQuery(id+"F26.imprint","IMPRINT",FACE,{"disambiguationData":[TD([[makeQuery(id+"F26.imprint","IMPRINT",EDGE,{"derivedFrom":sQuery(id+"F26.wireOp",EDGE,"E288")}),-1.0]])]});
            var Q25;
            Q25=makeQuery(id+"F27.imprint","IMPRINT",FACE,{"disambiguationData":[TD([[makeQuery(id+"F27.imprint","IMPRINT",EDGE,{"derivedFrom":sQuery(id+"F27.wireOp",EDGE,"E300")}),-1.0]])]});
            extrude(context, id + "F29", {"entities" : qUnion([Q0, Q1, Q2, Q3, Q4, Q5, Q6, Q7, Q8, Q9, Q10, Q11, Q12, Q13, Q14, Q15, Q16, Q17, Q18, Q19, Q20, Q21, Q22, Q23, Q24, Q25]), "operationType" : NewBodyOperationType.ADD, "depth" : (getVariable(context, 'ClipWidth')) * mm});
        }
        {
            var Q0;
            Q0=makeQuery(id+"F28.opExtrude","CAP_EDGE",EDGE,{"disambiguationData":[OSD([sQuery(id+"F2.wireOp",EDGE,"E10.sketch_text.stroke-3")])],"isStart":true});
            var Q1;
            Q1=makeQuery(id+"F28.opExtrude","CAP_EDGE",EDGE,{"disambiguationData":[OSD([sQuery(id+"F2.wireOp",EDGE,"E10.sketch_text.stroke-7")])],"isStart":true});
            var Q2;
            Q2=makeQuery(id+"F28.opExtrude","CAP_EDGE",EDGE,{"disambiguationData":[OSD([sQuery(id+"F3.wireOp",EDGE,"E22.sketch_text.stroke-10")])],"isStart":true});
            var Q3;
            Q3=makeQuery(id+"F28.opExtrude","CAP_EDGE",EDGE,{"disambiguationData":[OSD([sQuery(id+"F4.wireOp",EDGE,"E34.sketch_text.stroke-5")])],"isStart":true});
            var Q4;
            Q4=makeQuery(id+"F28.opExtrude","CAP_EDGE",EDGE,{"disambiguationData":[OSD([sQuery(id+"F5.wireOp",EDGE,"E46.sketch_text.stroke-2")])],"isStart":true});
            var Q5;
            Q5=makeQuery(id+"F28.opExtrude","CAP_EDGE",EDGE,{"disambiguationData":[OSD([sQuery(id+"F6.wireOp",EDGE,"E58.sketch_text.stroke-0")])],"isStart":true});
            var Q6;
            Q6=makeQuery(id+"F28.opExtrude","CAP_EDGE",EDGE,{"disambiguationData":[OSD([sQuery(id+"F7.wireOp",EDGE,"E70.sketch_text.stroke-0")])],"isStart":true});
            var Q7;
            Q7=makeQuery(id+"F28.opExtrude","CAP_EDGE",EDGE,{"disambiguationData":[OSD([sQuery(id+"F8.wireOp",EDGE,"E82.sketch_text.stroke-3")])],"isStart":true});
            var Q8;
            Q8=makeQuery(id+"F28.opExtrude","CAP_EDGE",EDGE,{"disambiguationData":[OSD([sQuery(id+"F9.wireOp",EDGE,"E94.sketch_text.stroke-4")])],"isStart":true});
            var Q9;
            Q9=makeQuery(id+"F28.opExtrude","CAP_EDGE",EDGE,{"disambiguationData":[OSD([sQuery(id+"F9.wireOp",EDGE,"E94.sketch_text.stroke-0")])],"isStart":true});
            var Q10;
            Q10=makeQuery(id+"F28.opExtrude","CAP_EDGE",EDGE,{"disambiguationData":[OSD([sQuery(id+"F10.wireOp",EDGE,"E106.sketch_text.stroke-3")])],"isStart":true});
            var Q11;
            Q11=makeQuery(id+"F28.opExtrude","CAP_EDGE",EDGE,{"disambiguationData":[OSD([sQuery(id+"F11.wireOp",EDGE,"E118.sketch_text.stroke-0")])],"isStart":true});
            var Q12;
            Q12=makeQuery(id+"F28.opExtrude","CAP_EDGE",EDGE,{"disambiguationData":[OSD([sQuery(id+"F12.wireOp",EDGE,"E130.sketch_text.stroke-4")])],"isStart":true});
            var Q13;
            Q13=makeQuery(id+"F28.opExtrude","CAP_EDGE",EDGE,{"disambiguationData":[OSD([sQuery(id+"F12.wireOp",EDGE,"E130.sketch_text.stroke-0")])],"isStart":true});
            var Q14;
            Q14=makeQuery(id+"F28.opExtrude","CAP_EDGE",EDGE,{"disambiguationData":[OSD([sQuery(id+"F13.wireOp",EDGE,"E142.sketch_text.stroke-5")])],"isStart":true});
            var Q15;
            Q15=makeQuery(id+"F28.opExtrude","CAP_EDGE",EDGE,{"disambiguationData":[OSD([sQuery(id+"F14.wireOp",EDGE,"E154.sketch_text.stroke-4")])],"isStart":true});
            var Q16;
            Q16=makeQuery(id+"F28.opExtrude","CAP_EDGE",EDGE,{"disambiguationData":[OSD([sQuery(id+"F14.wireOp",EDGE,"E154.sketch_text.stroke-18")])],"isStart":true});
            var Q17;
            Q17=makeQuery(id+"F28.opExtrude","CAP_EDGE",EDGE,{"disambiguationData":[OSD([sQuery(id+"F14.wireOp",EDGE,"E154.sketch_text.stroke-12")])],"isStart":true});
            var Q18;
            Q18=makeQuery(id+"F28.opExtrude","CAP_EDGE",EDGE,{"disambiguationData":[OSD([sQuery(id+"F15.wireOp",EDGE,"E166.sketch_text.stroke-5")])],"isStart":true});
            var Q19;
            Q19=makeQuery(id+"F28.opExtrude","CAP_EDGE",EDGE,{"disambiguationData":[OSD([sQuery(id+"F15.wireOp",EDGE,"E166.sketch_text.stroke-0")])],"isStart":true});
            var Q20;
            Q20=makeQuery(id+"F28.opExtrude","CAP_EDGE",EDGE,{"disambiguationData":[OSD([sQuery(id+"F16.wireOp",EDGE,"E178.sketch_text.stroke-2")])],"isStart":true});
            var Q21;
            Q21=makeQuery(id+"F28.opExtrude","CAP_EDGE",EDGE,{"disambiguationData":[OSD([sQuery(id+"F16.wireOp",EDGE,"E178.sketch_text.stroke-1")])],"isStart":true});
            var Q22;
            Q22=makeQuery(id+"F28.opExtrude","CAP_EDGE",EDGE,{"disambiguationData":[OSD([sQuery(id+"F17.wireOp",EDGE,"E190.sketch_text.stroke-11")])],"isStart":true});
            var Q23;
            Q23=makeQuery(id+"F28.opExtrude","CAP_EDGE",EDGE,{"disambiguationData":[OSD([sQuery(id+"F18.wireOp",EDGE,"E202.sketch_text.stroke-3")])],"isStart":true});
            var Q24;
            Q24=makeQuery(id+"F28.opExtrude","CAP_EDGE",EDGE,{"disambiguationData":[OSD([sQuery(id+"F19.wireOp",EDGE,"E214.sketch_text.stroke-8")])],"isStart":true});
            var Q25;
            Q25=makeQuery(id+"F28.opExtrude","CAP_EDGE",EDGE,{"disambiguationData":[OSD([sQuery(id+"F19.wireOp",EDGE,"E214.sketch_text.stroke-16")])],"isStart":true});
            var Q26;
            Q26=makeQuery(id+"F28.opExtrude","CAP_EDGE",EDGE,{"disambiguationData":[OSD([sQuery(id+"F20.wireOp",EDGE,"E226.sketch_text.stroke-2")])],"isStart":true});
            var Q27;
            Q27=makeQuery(id+"F28.opExtrude","CAP_EDGE",EDGE,{"disambiguationData":[OSD([sQuery(id+"F21.wireOp",EDGE,"E238.sketch_text.stroke-0")])],"isStart":true});
            var Q28;
            Q28=makeQuery(id+"F28.opExtrude","CAP_EDGE",EDGE,{"disambiguationData":[OSD([sQuery(id+"F22.wireOp",EDGE,"E250.sketch_text.stroke-4")])],"isStart":true});
            var Q29;
            Q29=makeQuery(id+"F28.opExtrude","CAP_EDGE",EDGE,{"disambiguationData":[OSD([sQuery(id+"F22.wireOp",EDGE,"E250.sketch_text.stroke-3")])],"isStart":true});
            var Q30;
            Q30=makeQuery(id+"F28.opExtrude","CAP_EDGE",EDGE,{"disambiguationData":[OSD([sQuery(id+"F23.wireOp",EDGE,"E262.sketch_text.stroke-2")])],"isStart":true});
            var Q31;
            Q31=makeQuery(id+"F28.opExtrude","CAP_EDGE",EDGE,{"disambiguationData":[OSD([sQuery(id+"F24.wireOp",EDGE,"E274.sketch_text.stroke-7")])],"isStart":true});
            var Q32;
            Q32=makeQuery(id+"F28.opExtrude","CAP_EDGE",EDGE,{"disambiguationData":[OSD([sQuery(id+"F24.wireOp",EDGE,"E274.sketch_text.stroke-0")])],"isStart":true});
            var Q33;
            Q33=makeQuery(id+"F28.opExtrude","CAP_EDGE",EDGE,{"disambiguationData":[OSD([sQuery(id+"F25.wireOp",EDGE,"E286.sketch_text.stroke-3")])],"isStart":true});
            var Q34;
            Q34=makeQuery(id+"F28.opExtrude","CAP_EDGE",EDGE,{"disambiguationData":[OSD([sQuery(id+"F25.wireOp",EDGE,"E286.sketch_text.stroke-0")])],"isStart":true});
            var Q35;
            Q35=makeQuery(id+"F28.opExtrude","CAP_EDGE",EDGE,{"disambiguationData":[OSD([sQuery(id+"F26.wireOp",EDGE,"E298.sketch_text.stroke-4")])],"isStart":true});
            var Q36;
            Q36=makeQuery(id+"F28.opExtrude","CAP_EDGE",EDGE,{"disambiguationData":[OSD([sQuery(id+"F27.wireOp",EDGE,"E310.sketch_text.stroke-0")])],"isStart":true});
            chamfer(context, id + "F30", {"entities" : qUnion([Q0, Q1, Q2, Q3, Q4, Q5, Q6, Q7, Q8, Q9, Q10, Q11, Q12, Q13, Q14, Q15, Q16, Q17, Q18, Q19, Q20, Q21, Q22, Q23, Q24, Q25, Q26, Q27, Q28, Q29, Q30, Q31, Q32, Q33, Q34, Q35, Q36]), "chamferType" : ChamferType.OFFSET_ANGLE, "width" : 1.5 * mm, "oppositeDirection" : false, "angle" : 45 * degree});
        }
        {
            var Q0;
            Q0=makeQuery(id+"F29.opExtrude","SWEPT_EDGE",EDGE,{"disambiguationData":[OSD([sQuery(id+"F2.wireOp",EDGE,"E0"),sQuery(id+"F2.wireOp",EDGE,"E4")])]});
            var Q1;
            Q1=makeQuery(id+"F29.opExtrude","SWEPT_EDGE",EDGE,{"disambiguationData":[OSD([sQuery(id+"F2.wireOp",EDGE,"E0"),sQuery(id+"F2.wireOp",EDGE,"E1")])]});
            var Q2;
            Q2=makeQuery(id+"F29.opExtrude","SWEPT_EDGE",EDGE,{"disambiguationData":[OSD([sQuery(id+"F3.wireOp",EDGE,"E12"),sQuery(id+"F3.wireOp",EDGE,"E16")])]});
            var Q3;
            Q3=makeQuery(id+"F29.opExtrude","SWEPT_EDGE",EDGE,{"disambiguationData":[OSD([sQuery(id+"F3.wireOp",EDGE,"E12"),sQuery(id+"F3.wireOp",EDGE,"E13")])]});
            var Q4;
            Q4=makeQuery(id+"F29.opExtrude","SWEPT_EDGE",EDGE,{"disambiguationData":[OSD([sQuery(id+"F7.wireOp",EDGE,"E60"),sQuery(id+"F7.wireOp",EDGE,"E61")])]});
            var Q5;
            Q5=makeQuery(id+"F29.opExtrude","SWEPT_EDGE",EDGE,{"disambiguationData":[OSD([sQuery(id+"F7.wireOp",EDGE,"E60"),sQuery(id+"F7.wireOp",EDGE,"E64")])]});
            var Q6;
            Q6=makeQuery(id+"F29.opExtrude","SWEPT_EDGE",EDGE,{"disambiguationData":[OSD([sQuery(id+"F8.wireOp",EDGE,"E72"),sQuery(id+"F8.wireOp",EDGE,"E76")])]});
            var Q7;
            Q7=makeQuery(id+"F29.opExtrude","SWEPT_EDGE",EDGE,{"disambiguationData":[OSD([sQuery(id+"F8.wireOp",EDGE,"E72"),sQuery(id+"F8.wireOp",EDGE,"E73")])]});
            var Q8;
            Q8=makeQuery(id+"F29.opExtrude","SWEPT_EDGE",EDGE,{"disambiguationData":[OSD([sQuery(id+"F9.wireOp",EDGE,"E84"),sQuery(id+"F9.wireOp",EDGE,"E88")])]});
            var Q9;
            Q9=makeQuery(id+"F29.opExtrude","SWEPT_EDGE",EDGE,{"disambiguationData":[OSD([sQuery(id+"F4.wireOp",EDGE,"E24"),sQuery(id+"F4.wireOp",EDGE,"E28")])]});
            var Q10;
            Q10=makeQuery(id+"F29.opExtrude","SWEPT_EDGE",EDGE,{"disambiguationData":[OSD([sQuery(id+"F9.wireOp",EDGE,"E84"),sQuery(id+"F9.wireOp",EDGE,"E85")])]});
            var Q11;
            Q11=makeQuery(id+"F29.opExtrude","SWEPT_EDGE",EDGE,{"disambiguationData":[OSD([sQuery(id+"F4.wireOp",EDGE,"E24"),sQuery(id+"F4.wireOp",EDGE,"E25")])]});
            var Q12;
            Q12=makeQuery(id+"F29.opExtrude","SWEPT_EDGE",EDGE,{"disambiguationData":[OSD([sQuery(id+"F10.wireOp",EDGE,"E96"),sQuery(id+"F10.wireOp",EDGE,"E100")])]});
            var Q13;
            Q13=makeQuery(id+"F29.opExtrude","SWEPT_EDGE",EDGE,{"disambiguationData":[OSD([sQuery(id+"F5.wireOp",EDGE,"E36"),sQuery(id+"F5.wireOp",EDGE,"E40")])]});
            var Q14;
            Q14=makeQuery(id+"F29.opExtrude","SWEPT_EDGE",EDGE,{"disambiguationData":[OSD([sQuery(id+"F10.wireOp",EDGE,"E96"),sQuery(id+"F10.wireOp",EDGE,"E97")])]});
            var Q15;
            Q15=makeQuery(id+"F29.opExtrude","SWEPT_EDGE",EDGE,{"disambiguationData":[OSD([sQuery(id+"F5.wireOp",EDGE,"E36"),sQuery(id+"F5.wireOp",EDGE,"E37")])]});
            var Q16;
            Q16=makeQuery(id+"F29.opExtrude","SWEPT_EDGE",EDGE,{"disambiguationData":[OSD([sQuery(id+"F6.wireOp",EDGE,"E48"),sQuery(id+"F6.wireOp",EDGE,"E52")])]});
            var Q17;
            Q17=makeQuery(id+"F29.opExtrude","SWEPT_EDGE",EDGE,{"disambiguationData":[OSD([sQuery(id+"F11.wireOp",EDGE,"E108"),sQuery(id+"F11.wireOp",EDGE,"E112")])]});
            var Q18;
            Q18=makeQuery(id+"F29.opExtrude","SWEPT_EDGE",EDGE,{"disambiguationData":[OSD([sQuery(id+"F11.wireOp",EDGE,"E108"),sQuery(id+"F11.wireOp",EDGE,"E109")])]});
            var Q19;
            Q19=makeQuery(id+"F29.opExtrude","SWEPT_EDGE",EDGE,{"disambiguationData":[OSD([sQuery(id+"F6.wireOp",EDGE,"E48"),sQuery(id+"F6.wireOp",EDGE,"E49")])]});
            var Q20;
            Q20=makeQuery(id+"F29.opExtrude","SWEPT_EDGE",EDGE,{"disambiguationData":[OSD([sQuery(id+"F27.wireOp",EDGE,"E300"),sQuery(id+"F27.wireOp",EDGE,"E301")])]});
            var Q21;
            Q21=makeQuery(id+"F29.opExtrude","SWEPT_EDGE",EDGE,{"disambiguationData":[OSD([sQuery(id+"F27.wireOp",EDGE,"E300"),sQuery(id+"F27.wireOp",EDGE,"E304")])]});
            var Q22;
            Q22=makeQuery(id+"F29.opExtrude","SWEPT_EDGE",EDGE,{"disambiguationData":[OSD([sQuery(id+"F16.wireOp",EDGE,"E168"),sQuery(id+"F16.wireOp",EDGE,"E169")])]});
            var Q23;
            Q23=makeQuery(id+"F29.opExtrude","SWEPT_EDGE",EDGE,{"disambiguationData":[OSD([sQuery(id+"F21.wireOp",EDGE,"E228"),sQuery(id+"F21.wireOp",EDGE,"E229")])]});
            var Q24;
            Q24=makeQuery(id+"F29.opExtrude","SWEPT_EDGE",EDGE,{"disambiguationData":[OSD([sQuery(id+"F21.wireOp",EDGE,"E228"),sQuery(id+"F21.wireOp",EDGE,"E232")])]});
            var Q25;
            Q25=makeQuery(id+"F29.opExtrude","SWEPT_EDGE",EDGE,{"disambiguationData":[OSD([sQuery(id+"F16.wireOp",EDGE,"E168"),sQuery(id+"F16.wireOp",EDGE,"E172")])]});
            var Q26;
            Q26=makeQuery(id+"F29.opExtrude","SWEPT_EDGE",EDGE,{"disambiguationData":[OSD([sQuery(id+"F15.wireOp",EDGE,"E156"),sQuery(id+"F15.wireOp",EDGE,"E157")])]});
            var Q27;
            Q27=makeQuery(id+"F29.opExtrude","SWEPT_EDGE",EDGE,{"disambiguationData":[OSD([sQuery(id+"F20.wireOp",EDGE,"E216"),sQuery(id+"F20.wireOp",EDGE,"E217")])]});
            var Q28;
            Q28=makeQuery(id+"F29.opExtrude","SWEPT_EDGE",EDGE,{"disambiguationData":[OSD([sQuery(id+"F20.wireOp",EDGE,"E216"),sQuery(id+"F20.wireOp",EDGE,"E220")])]});
            var Q29;
            Q29=makeQuery(id+"F29.opExtrude","SWEPT_EDGE",EDGE,{"disambiguationData":[OSD([sQuery(id+"F19.wireOp",EDGE,"E204"),sQuery(id+"F19.wireOp",EDGE,"E205")])]});
            var Q30;
            Q30=makeQuery(id+"F29.opExtrude","SWEPT_EDGE",EDGE,{"disambiguationData":[OSD([sQuery(id+"F15.wireOp",EDGE,"E156"),sQuery(id+"F15.wireOp",EDGE,"E160")])]});
            var Q31;
            Q31=makeQuery(id+"F29.opExtrude","SWEPT_EDGE",EDGE,{"disambiguationData":[OSD([sQuery(id+"F14.wireOp",EDGE,"E144"),sQuery(id+"F14.wireOp",EDGE,"E145")])]});
            var Q32;
            Q32=makeQuery(id+"F29.opExtrude","SWEPT_EDGE",EDGE,{"disambiguationData":[OSD([sQuery(id+"F19.wireOp",EDGE,"E204"),sQuery(id+"F19.wireOp",EDGE,"E208")])]});
            var Q33;
            Q33=makeQuery(id+"F29.opExtrude","SWEPT_EDGE",EDGE,{"disambiguationData":[OSD([sQuery(id+"F14.wireOp",EDGE,"E144"),sQuery(id+"F14.wireOp",EDGE,"E148")])]});
            var Q34;
            Q34=makeQuery(id+"F29.opExtrude","SWEPT_EDGE",EDGE,{"disambiguationData":[OSD([sQuery(id+"F13.wireOp",EDGE,"E132"),sQuery(id+"F13.wireOp",EDGE,"E133")])]});
            var Q35;
            Q35=makeQuery(id+"F29.opExtrude","SWEPT_EDGE",EDGE,{"disambiguationData":[OSD([sQuery(id+"F18.wireOp",EDGE,"E192"),sQuery(id+"F18.wireOp",EDGE,"E193")])]});
            var Q36;
            Q36=makeQuery(id+"F29.opExtrude","SWEPT_EDGE",EDGE,{"disambiguationData":[OSD([sQuery(id+"F18.wireOp",EDGE,"E192"),sQuery(id+"F18.wireOp",EDGE,"E196")])]});
            var Q37;
            Q37=makeQuery(id+"F29.opExtrude","SWEPT_EDGE",EDGE,{"disambiguationData":[OSD([sQuery(id+"F17.wireOp",EDGE,"E180"),sQuery(id+"F17.wireOp",EDGE,"E181")])]});
            var Q38;
            Q38=makeQuery(id+"F29.opExtrude","SWEPT_EDGE",EDGE,{"disambiguationData":[OSD([sQuery(id+"F13.wireOp",EDGE,"E132"),sQuery(id+"F13.wireOp",EDGE,"E136")])]});
            var Q39;
            Q39=makeQuery(id+"F29.opExtrude","SWEPT_EDGE",EDGE,{"disambiguationData":[OSD([sQuery(id+"F12.wireOp",EDGE,"E120"),sQuery(id+"F12.wireOp",EDGE,"E121")])]});
            var Q40;
            Q40=makeQuery(id+"F29.opExtrude","SWEPT_EDGE",EDGE,{"disambiguationData":[OSD([sQuery(id+"F12.wireOp",EDGE,"E120"),sQuery(id+"F12.wireOp",EDGE,"E124")])]});
            var Q41;
            Q41=makeQuery(id+"F29.opExtrude","SWEPT_EDGE",EDGE,{"disambiguationData":[OSD([sQuery(id+"F17.wireOp",EDGE,"E180"),sQuery(id+"F17.wireOp",EDGE,"E184")])]});
            var Q42;
            Q42=makeQuery(id+"F29.opExtrude","SWEPT_EDGE",EDGE,{"disambiguationData":[OSD([sQuery(id+"F22.wireOp",EDGE,"E240"),sQuery(id+"F22.wireOp",EDGE,"E244")])]});
            var Q43;
            Q43=makeQuery(id+"F29.opExtrude","SWEPT_EDGE",EDGE,{"disambiguationData":[OSD([sQuery(id+"F22.wireOp",EDGE,"E240"),sQuery(id+"F22.wireOp",EDGE,"E241")])]});
            var Q44;
            Q44=makeQuery(id+"F29.opExtrude","SWEPT_EDGE",EDGE,{"disambiguationData":[OSD([sQuery(id+"F23.wireOp",EDGE,"E252"),sQuery(id+"F23.wireOp",EDGE,"E256")])]});
            var Q45;
            Q45=makeQuery(id+"F29.opExtrude","SWEPT_EDGE",EDGE,{"disambiguationData":[OSD([sQuery(id+"F23.wireOp",EDGE,"E252"),sQuery(id+"F23.wireOp",EDGE,"E253")])]});
            var Q46;
            Q46=makeQuery(id+"F29.opExtrude","SWEPT_EDGE",EDGE,{"disambiguationData":[OSD([sQuery(id+"F24.wireOp",EDGE,"E264"),sQuery(id+"F24.wireOp",EDGE,"E268")])]});
            var Q47;
            Q47=makeQuery(id+"F29.opExtrude","SWEPT_EDGE",EDGE,{"disambiguationData":[OSD([sQuery(id+"F24.wireOp",EDGE,"E264"),sQuery(id+"F24.wireOp",EDGE,"E265")])]});
            var Q48;
            Q48=makeQuery(id+"F29.opExtrude","SWEPT_EDGE",EDGE,{"disambiguationData":[OSD([sQuery(id+"F25.wireOp",EDGE,"E276"),sQuery(id+"F25.wireOp",EDGE,"E280")])]});
            var Q49;
            Q49=makeQuery(id+"F29.opExtrude","SWEPT_EDGE",EDGE,{"disambiguationData":[OSD([sQuery(id+"F25.wireOp",EDGE,"E276"),sQuery(id+"F25.wireOp",EDGE,"E277")])]});
            var Q50;
            Q50=makeQuery(id+"F29.opExtrude","SWEPT_EDGE",EDGE,{"disambiguationData":[OSD([sQuery(id+"F26.wireOp",EDGE,"E288"),sQuery(id+"F26.wireOp",EDGE,"E292")])]});
            var Q51;
            Q51=makeQuery(id+"F29.opExtrude","SWEPT_EDGE",EDGE,{"disambiguationData":[OSD([sQuery(id+"F26.wireOp",EDGE,"E288"),sQuery(id+"F26.wireOp",EDGE,"E289")])]});
            var Q52;
            Q52=makeQuery(id+"F29.opExtrude","SWEPT_EDGE",EDGE,{"disambiguationData":[OSD([sQuery(id+"F2.wireOp",EDGE,"E3"),sQuery(id+"F2.wireOp",EDGE,"E4")])]});
            var Q53;
            Q53=makeQuery(id+"F29.opExtrude","SWEPT_EDGE",EDGE,{"disambiguationData":[OSD([sQuery(id+"F3.wireOp",EDGE,"E15"),sQuery(id+"F3.wireOp",EDGE,"E16")])]});
            var Q54;
            Q54=makeQuery(id+"F29.opExtrude","SWEPT_EDGE",EDGE,{"disambiguationData":[OSD([sQuery(id+"F4.wireOp",EDGE,"E27"),sQuery(id+"F4.wireOp",EDGE,"E28")])]});
            var Q55;
            Q55=makeQuery(id+"F29.opExtrude","SWEPT_EDGE",EDGE,{"disambiguationData":[OSD([sQuery(id+"F5.wireOp",EDGE,"E39"),sQuery(id+"F5.wireOp",EDGE,"E40")])]});
            var Q56;
            Q56=makeQuery(id+"F29.opExtrude","SWEPT_EDGE",EDGE,{"disambiguationData":[OSD([sQuery(id+"F6.wireOp",EDGE,"E51"),sQuery(id+"F6.wireOp",EDGE,"E52")])]});
            var Q57;
            Q57=makeQuery(id+"F29.opExtrude","SWEPT_EDGE",EDGE,{"disambiguationData":[OSD([sQuery(id+"F7.wireOp",EDGE,"E63"),sQuery(id+"F7.wireOp",EDGE,"E64")])]});
            var Q58;
            Q58=makeQuery(id+"F29.opExtrude","SWEPT_EDGE",EDGE,{"disambiguationData":[OSD([sQuery(id+"F8.wireOp",EDGE,"E75"),sQuery(id+"F8.wireOp",EDGE,"E76")])]});
            var Q59;
            Q59=makeQuery(id+"F29.opExtrude","SWEPT_EDGE",EDGE,{"disambiguationData":[OSD([sQuery(id+"F9.wireOp",EDGE,"E87"),sQuery(id+"F9.wireOp",EDGE,"E88")])]});
            var Q60;
            Q60=makeQuery(id+"F29.opExtrude","SWEPT_EDGE",EDGE,{"disambiguationData":[OSD([sQuery(id+"F10.wireOp",EDGE,"E99"),sQuery(id+"F10.wireOp",EDGE,"E100")])]});
            var Q61;
            Q61=makeQuery(id+"F29.opExtrude","SWEPT_EDGE",EDGE,{"disambiguationData":[OSD([sQuery(id+"F11.wireOp",EDGE,"E111"),sQuery(id+"F11.wireOp",EDGE,"E112")])]});
            var Q62;
            Q62=makeQuery(id+"F29.opExtrude","SWEPT_EDGE",EDGE,{"disambiguationData":[OSD([sQuery(id+"F12.wireOp",EDGE,"E123"),sQuery(id+"F12.wireOp",EDGE,"E124")])]});
            var Q63;
            Q63=makeQuery(id+"F29.opExtrude","SWEPT_EDGE",EDGE,{"disambiguationData":[OSD([sQuery(id+"F13.wireOp",EDGE,"E135"),sQuery(id+"F13.wireOp",EDGE,"E136")])]});
            var Q64;
            Q64=makeQuery(id+"F29.opExtrude","SWEPT_EDGE",EDGE,{"disambiguationData":[OSD([sQuery(id+"F14.wireOp",EDGE,"E147"),sQuery(id+"F14.wireOp",EDGE,"E148")])]});
            var Q65;
            Q65=makeQuery(id+"F29.opExtrude","SWEPT_EDGE",EDGE,{"disambiguationData":[OSD([sQuery(id+"F15.wireOp",EDGE,"E159"),sQuery(id+"F15.wireOp",EDGE,"E160")])]});
            var Q66;
            Q66=makeQuery(id+"F29.opExtrude","SWEPT_EDGE",EDGE,{"disambiguationData":[OSD([sQuery(id+"F16.wireOp",EDGE,"E171"),sQuery(id+"F16.wireOp",EDGE,"E172")])]});
            var Q67;
            Q67=makeQuery(id+"F29.opExtrude","SWEPT_EDGE",EDGE,{"disambiguationData":[OSD([sQuery(id+"F17.wireOp",EDGE,"E183"),sQuery(id+"F17.wireOp",EDGE,"E184")])]});
            var Q68;
            Q68=makeQuery(id+"F29.opExtrude","SWEPT_EDGE",EDGE,{"disambiguationData":[OSD([sQuery(id+"F19.wireOp",EDGE,"E207"),sQuery(id+"F19.wireOp",EDGE,"E208")])]});
            var Q69;
            Q69=makeQuery(id+"F29.opExtrude","SWEPT_EDGE",EDGE,{"disambiguationData":[OSD([sQuery(id+"F20.wireOp",EDGE,"E219"),sQuery(id+"F20.wireOp",EDGE,"E220")])]});
            var Q70;
            Q70=makeQuery(id+"F29.opExtrude","SWEPT_EDGE",EDGE,{"disambiguationData":[OSD([sQuery(id+"F21.wireOp",EDGE,"E231"),sQuery(id+"F21.wireOp",EDGE,"E232")])]});
            var Q71;
            Q71=makeQuery(id+"F29.opExtrude","SWEPT_EDGE",EDGE,{"disambiguationData":[OSD([sQuery(id+"F22.wireOp",EDGE,"E243"),sQuery(id+"F22.wireOp",EDGE,"E244")])]});
            var Q72;
            Q72=makeQuery(id+"F29.opExtrude","SWEPT_EDGE",EDGE,{"disambiguationData":[OSD([sQuery(id+"F23.wireOp",EDGE,"E255"),sQuery(id+"F23.wireOp",EDGE,"E256")])]});
            var Q73;
            Q73=makeQuery(id+"F29.opExtrude","SWEPT_EDGE",EDGE,{"disambiguationData":[OSD([sQuery(id+"F24.wireOp",EDGE,"E267"),sQuery(id+"F24.wireOp",EDGE,"E268")])]});
            var Q74;
            Q74=makeQuery(id+"F29.opExtrude","SWEPT_EDGE",EDGE,{"disambiguationData":[OSD([sQuery(id+"F25.wireOp",EDGE,"E279"),sQuery(id+"F25.wireOp",EDGE,"E280")])]});
            var Q75;
            Q75=makeQuery(id+"F29.opExtrude","SWEPT_EDGE",EDGE,{"disambiguationData":[OSD([sQuery(id+"F26.wireOp",EDGE,"E291"),sQuery(id+"F26.wireOp",EDGE,"E292")])]});
            var Q76;
            Q76=makeQuery(id+"F29.opExtrude","SWEPT_EDGE",EDGE,{"disambiguationData":[OSD([sQuery(id+"F22.wireOp",EDGE,"E241"),sQuery(id+"F22.wireOp",EDGE,"E242")])]});
            var Q77;
            Q77=makeQuery(id+"F29.opExtrude","SWEPT_EDGE",EDGE,{"disambiguationData":[OSD([sQuery(id+"F23.wireOp",EDGE,"E253"),sQuery(id+"F23.wireOp",EDGE,"E254")])]});
            var Q78;
            Q78=makeQuery(id+"F29.opExtrude","SWEPT_EDGE",EDGE,{"disambiguationData":[OSD([sQuery(id+"F24.wireOp",EDGE,"E265"),sQuery(id+"F24.wireOp",EDGE,"E266")])]});
            var Q79;
            Q79=makeQuery(id+"F29.opExtrude","SWEPT_EDGE",EDGE,{"disambiguationData":[OSD([sQuery(id+"F25.wireOp",EDGE,"E277"),sQuery(id+"F25.wireOp",EDGE,"E278")])]});
            var Q80;
            Q80=makeQuery(id+"F29.opExtrude","SWEPT_EDGE",EDGE,{"disambiguationData":[OSD([sQuery(id+"F26.wireOp",EDGE,"E289"),sQuery(id+"F26.wireOp",EDGE,"E290")])]});
            var Q81;
            Q81=makeQuery(id+"F29.opExtrude","SWEPT_EDGE",EDGE,{"disambiguationData":[OSD([sQuery(id+"F17.wireOp",EDGE,"E181"),sQuery(id+"F17.wireOp",EDGE,"E182")])]});
            var Q82;
            Q82=makeQuery(id+"F29.opExtrude","SWEPT_EDGE",EDGE,{"disambiguationData":[OSD([sQuery(id+"F18.wireOp",EDGE,"E193"),sQuery(id+"F18.wireOp",EDGE,"E194")])]});
            var Q83;
            Q83=makeQuery(id+"F29.opExtrude","SWEPT_EDGE",EDGE,{"disambiguationData":[OSD([sQuery(id+"F19.wireOp",EDGE,"E205"),sQuery(id+"F19.wireOp",EDGE,"E206")])]});
            var Q84;
            Q84=makeQuery(id+"F29.opExtrude","SWEPT_EDGE",EDGE,{"disambiguationData":[OSD([sQuery(id+"F20.wireOp",EDGE,"E217"),sQuery(id+"F20.wireOp",EDGE,"E218")])]});
            var Q85;
            Q85=makeQuery(id+"F29.opExtrude","SWEPT_EDGE",EDGE,{"disambiguationData":[OSD([sQuery(id+"F21.wireOp",EDGE,"E229"),sQuery(id+"F21.wireOp",EDGE,"E230")])]});
            var Q86;
            Q86=makeQuery(id+"F29.opExtrude","SWEPT_EDGE",EDGE,{"disambiguationData":[OSD([sQuery(id+"F12.wireOp",EDGE,"E121"),sQuery(id+"F12.wireOp",EDGE,"E122")])]});
            var Q87;
            Q87=makeQuery(id+"F29.opExtrude","SWEPT_EDGE",EDGE,{"disambiguationData":[OSD([sQuery(id+"F13.wireOp",EDGE,"E133"),sQuery(id+"F13.wireOp",EDGE,"E134")])]});
            var Q88;
            Q88=makeQuery(id+"F29.opExtrude","SWEPT_EDGE",EDGE,{"disambiguationData":[OSD([sQuery(id+"F15.wireOp",EDGE,"E157"),sQuery(id+"F15.wireOp",EDGE,"E158")])]});
            var Q89;
            Q89=makeQuery(id+"F29.opExtrude","SWEPT_EDGE",EDGE,{"disambiguationData":[OSD([sQuery(id+"F16.wireOp",EDGE,"E169"),sQuery(id+"F16.wireOp",EDGE,"E170")])]});
            var Q90;
            Q90=makeQuery(id+"F29.opExtrude","SWEPT_EDGE",EDGE,{"disambiguationData":[OSD([sQuery(id+"F27.wireOp",EDGE,"E301"),sQuery(id+"F27.wireOp",EDGE,"E302")])]});
            var Q91;
            Q91=makeQuery(id+"F29.opExtrude","SWEPT_EDGE",EDGE,{"disambiguationData":[OSD([sQuery(id+"F7.wireOp",EDGE,"E61"),sQuery(id+"F7.wireOp",EDGE,"E62")])]});
            var Q92;
            Q92=makeQuery(id+"F29.opExtrude","SWEPT_EDGE",EDGE,{"disambiguationData":[OSD([sQuery(id+"F8.wireOp",EDGE,"E73"),sQuery(id+"F8.wireOp",EDGE,"E74")])]});
            var Q93;
            Q93=makeQuery(id+"F29.opExtrude","SWEPT_EDGE",EDGE,{"disambiguationData":[OSD([sQuery(id+"F9.wireOp",EDGE,"E85"),sQuery(id+"F9.wireOp",EDGE,"E86")])]});
            var Q94;
            Q94=makeQuery(id+"F29.opExtrude","SWEPT_EDGE",EDGE,{"disambiguationData":[OSD([sQuery(id+"F10.wireOp",EDGE,"E97"),sQuery(id+"F10.wireOp",EDGE,"E98")])]});
            var Q95;
            Q95=makeQuery(id+"F29.opExtrude","SWEPT_EDGE",EDGE,{"disambiguationData":[OSD([sQuery(id+"F11.wireOp",EDGE,"E109"),sQuery(id+"F11.wireOp",EDGE,"E110")])]});
            var Q96;
            Q96=makeQuery(id+"F29.opExtrude","SWEPT_EDGE",EDGE,{"disambiguationData":[OSD([sQuery(id+"F2.wireOp",EDGE,"E1"),sQuery(id+"F2.wireOp",EDGE,"E2")])]});
            var Q97;
            Q97=makeQuery(id+"F29.opExtrude","SWEPT_EDGE",EDGE,{"disambiguationData":[OSD([sQuery(id+"F3.wireOp",EDGE,"E13"),sQuery(id+"F3.wireOp",EDGE,"E14")])]});
            var Q98;
            Q98=makeQuery(id+"F29.opExtrude","SWEPT_EDGE",EDGE,{"disambiguationData":[OSD([sQuery(id+"F4.wireOp",EDGE,"E25"),sQuery(id+"F4.wireOp",EDGE,"E26")])]});
            var Q99;
            Q99=makeQuery(id+"F29.opExtrude","SWEPT_EDGE",EDGE,{"disambiguationData":[OSD([sQuery(id+"F5.wireOp",EDGE,"E37"),sQuery(id+"F5.wireOp",EDGE,"E38")])]});
            var Q100;
            Q100=makeQuery(id+"F29.opExtrude","SWEPT_EDGE",EDGE,{"disambiguationData":[OSD([sQuery(id+"F6.wireOp",EDGE,"E49"),sQuery(id+"F6.wireOp",EDGE,"E50")])]});
            var Q101;
            Q101=makeQuery(id+"F29.opExtrude","SWEPT_EDGE",EDGE,{"disambiguationData":[OSD([sQuery(id+"F2.wireOp",EDGE,"E5"),sQuery(id+"F2.wireOp",EDGE,"E9")])]});
            var Q102;
            Q102=makeQuery(id+"F29.opExtrude","SWEPT_EDGE",EDGE,{"disambiguationData":[OSD([sQuery(id+"F2.wireOp",EDGE,"E5"),sQuery(id+"F2.wireOp",EDGE,"E6")])]});
            var Q103;
            Q103=makeQuery(id+"F29.opExtrude","SWEPT_EDGE",EDGE,{"disambiguationData":[OSD([sQuery(id+"F2.wireOp",EDGE,"E8"),sQuery(id+"F2.wireOp",EDGE,"E9")])]});
            var Q104;
            Q104=makeQuery(id+"F29.opExtrude","SWEPT_EDGE",EDGE,{"disambiguationData":[OSD([sQuery(id+"F2.wireOp",EDGE,"E6"),sQuery(id+"F2.wireOp",EDGE,"E7")])]});
            var Q105;
            Q105=makeQuery(id+"F29.opExtrude","SWEPT_EDGE",EDGE,{"disambiguationData":[OSD([sQuery(id+"F2.wireOp",EDGE,"E7"),sQuery(id+"F2.wireOp",EDGE,"E8")])]});
            var Q106;
            Q106=makeQuery(id+"F29.opExtrude","SWEPT_EDGE",EDGE,{"disambiguationData":[OSD([sQuery(id+"F2.wireOp",EDGE,"E2"),sQuery(id+"F2.wireOp",EDGE,"E3")])]});
            var Q107;
            Q107=makeQuery(id+"F29.opExtrude","SWEPT_EDGE",EDGE,{"disambiguationData":[OSD([sQuery(id+"F3.wireOp",EDGE,"E14"),sQuery(id+"F3.wireOp",EDGE,"E15")])]});
            var Q108;
            Q108=makeQuery(id+"F29.opExtrude","SWEPT_EDGE",EDGE,{"disambiguationData":[OSD([sQuery(id+"F4.wireOp",EDGE,"E26"),sQuery(id+"F4.wireOp",EDGE,"E27")])]});
            var Q109;
            Q109=makeQuery(id+"F29.opExtrude","SWEPT_EDGE",EDGE,{"disambiguationData":[OSD([sQuery(id+"F5.wireOp",EDGE,"E38"),sQuery(id+"F5.wireOp",EDGE,"E39")])]});
            var Q110;
            Q110=makeQuery(id+"F29.opExtrude","SWEPT_EDGE",EDGE,{"disambiguationData":[OSD([sQuery(id+"F6.wireOp",EDGE,"E50"),sQuery(id+"F6.wireOp",EDGE,"E51")])]});
            var Q111;
            Q111=makeQuery(id+"F29.opExtrude","SWEPT_EDGE",EDGE,{"disambiguationData":[OSD([sQuery(id+"F7.wireOp",EDGE,"E62"),sQuery(id+"F7.wireOp",EDGE,"E63")])]});
            var Q112;
            Q112=makeQuery(id+"F29.opExtrude","SWEPT_EDGE",EDGE,{"disambiguationData":[OSD([sQuery(id+"F8.wireOp",EDGE,"E74"),sQuery(id+"F8.wireOp",EDGE,"E75")])]});
            var Q113;
            Q113=makeQuery(id+"F29.opExtrude","SWEPT_EDGE",EDGE,{"disambiguationData":[OSD([sQuery(id+"F9.wireOp",EDGE,"E86"),sQuery(id+"F9.wireOp",EDGE,"E87")])]});
            var Q114;
            Q114=makeQuery(id+"F29.opExtrude","SWEPT_EDGE",EDGE,{"disambiguationData":[OSD([sQuery(id+"F10.wireOp",EDGE,"E98"),sQuery(id+"F10.wireOp",EDGE,"E99")])]});
            var Q115;
            Q115=makeQuery(id+"F29.opExtrude","SWEPT_EDGE",EDGE,{"disambiguationData":[OSD([sQuery(id+"F11.wireOp",EDGE,"E110"),sQuery(id+"F11.wireOp",EDGE,"E111")])]});
            var Q116;
            Q116=makeQuery(id+"F29.opExtrude","SWEPT_EDGE",EDGE,{"disambiguationData":[OSD([sQuery(id+"F12.wireOp",EDGE,"E122"),sQuery(id+"F12.wireOp",EDGE,"E123")])]});
            var Q117;
            Q117=makeQuery(id+"F29.opExtrude","SWEPT_EDGE",EDGE,{"disambiguationData":[OSD([sQuery(id+"F13.wireOp",EDGE,"E134"),sQuery(id+"F13.wireOp",EDGE,"E135")])]});
            var Q118;
            Q118=makeQuery(id+"F29.opExtrude","SWEPT_EDGE",EDGE,{"disambiguationData":[OSD([sQuery(id+"F14.wireOp",EDGE,"E146"),sQuery(id+"F14.wireOp",EDGE,"E147")])]});
            var Q119;
            Q119=makeQuery(id+"F29.opExtrude","SWEPT_EDGE",EDGE,{"disambiguationData":[OSD([sQuery(id+"F15.wireOp",EDGE,"E158"),sQuery(id+"F15.wireOp",EDGE,"E159")])]});
            var Q120;
            Q120=makeQuery(id+"F29.opExtrude","SWEPT_EDGE",EDGE,{"disambiguationData":[OSD([sQuery(id+"F16.wireOp",EDGE,"E170"),sQuery(id+"F16.wireOp",EDGE,"E171")])]});
            var Q121;
            Q121=makeQuery(id+"F29.opExtrude","SWEPT_EDGE",EDGE,{"disambiguationData":[OSD([sQuery(id+"F21.wireOp",EDGE,"E230"),sQuery(id+"F21.wireOp",EDGE,"E231")])]});
            var Q122;
            Q122=makeQuery(id+"F29.opExtrude","SWEPT_EDGE",EDGE,{"disambiguationData":[OSD([sQuery(id+"F20.wireOp",EDGE,"E218"),sQuery(id+"F20.wireOp",EDGE,"E219")])]});
            var Q123;
            Q123=makeQuery(id+"F29.opExtrude","SWEPT_EDGE",EDGE,{"disambiguationData":[OSD([sQuery(id+"F19.wireOp",EDGE,"E206"),sQuery(id+"F19.wireOp",EDGE,"E207")])]});
            var Q124;
            Q124=makeQuery(id+"F29.opExtrude","SWEPT_EDGE",EDGE,{"disambiguationData":[OSD([sQuery(id+"F18.wireOp",EDGE,"E194"),sQuery(id+"F18.wireOp",EDGE,"E195")])]});
            var Q125;
            Q125=makeQuery(id+"F29.opExtrude","SWEPT_EDGE",EDGE,{"disambiguationData":[OSD([sQuery(id+"F17.wireOp",EDGE,"E182"),sQuery(id+"F17.wireOp",EDGE,"E183")])]});
            var Q126;
            Q126=makeQuery(id+"F29.opExtrude","SWEPT_EDGE",EDGE,{"disambiguationData":[OSD([sQuery(id+"F22.wireOp",EDGE,"E242"),sQuery(id+"F22.wireOp",EDGE,"E243")])]});
            var Q127;
            Q127=makeQuery(id+"F29.opExtrude","SWEPT_EDGE",EDGE,{"disambiguationData":[OSD([sQuery(id+"F23.wireOp",EDGE,"E254"),sQuery(id+"F23.wireOp",EDGE,"E255")])]});
            var Q128;
            Q128=makeQuery(id+"F29.opExtrude","SWEPT_EDGE",EDGE,{"disambiguationData":[OSD([sQuery(id+"F24.wireOp",EDGE,"E266"),sQuery(id+"F24.wireOp",EDGE,"E267")])]});
            var Q129;
            Q129=makeQuery(id+"F29.opExtrude","SWEPT_EDGE",EDGE,{"disambiguationData":[OSD([sQuery(id+"F25.wireOp",EDGE,"E278"),sQuery(id+"F25.wireOp",EDGE,"E279")])]});
            var Q130;
            Q130=makeQuery(id+"F29.opExtrude","SWEPT_EDGE",EDGE,{"disambiguationData":[OSD([sQuery(id+"F26.wireOp",EDGE,"E290"),sQuery(id+"F26.wireOp",EDGE,"E291")])]});
            var Q131;
            Q131=makeQuery(id+"F29.opExtrude","SWEPT_EDGE",EDGE,{"disambiguationData":[OSD([sQuery(id+"F27.wireOp",EDGE,"E302"),sQuery(id+"F27.wireOp",EDGE,"E303")])]});
            var Q132;
            Q132=makeQuery(id+"F29.opExtrude","SWEPT_EDGE",EDGE,{"disambiguationData":[OSD([sQuery(id+"F3.wireOp",EDGE,"E17"),sQuery(id+"F3.wireOp",EDGE,"E21")])]});
            var Q133;
            Q133=makeQuery(id+"F29.opExtrude","SWEPT_EDGE",EDGE,{"disambiguationData":[OSD([sQuery(id+"F4.wireOp",EDGE,"E29"),sQuery(id+"F4.wireOp",EDGE,"E33")])]});
            var Q134;
            Q134=makeQuery(id+"F29.opExtrude","SWEPT_EDGE",EDGE,{"disambiguationData":[OSD([sQuery(id+"F5.wireOp",EDGE,"E41"),sQuery(id+"F5.wireOp",EDGE,"E45")])]});
            var Q135;
            Q135=makeQuery(id+"F29.opExtrude","SWEPT_EDGE",EDGE,{"disambiguationData":[OSD([sQuery(id+"F6.wireOp",EDGE,"E53"),sQuery(id+"F6.wireOp",EDGE,"E57")])]});
            var Q136;
            Q136=makeQuery(id+"F29.opExtrude","SWEPT_EDGE",EDGE,{"disambiguationData":[OSD([sQuery(id+"F11.wireOp",EDGE,"E113"),sQuery(id+"F11.wireOp",EDGE,"E117")])]});
            var Q137;
            Q137=makeQuery(id+"F29.opExtrude","SWEPT_EDGE",EDGE,{"disambiguationData":[OSD([sQuery(id+"F10.wireOp",EDGE,"E101"),sQuery(id+"F10.wireOp",EDGE,"E105")])]});
            var Q138;
            Q138=makeQuery(id+"F29.opExtrude","SWEPT_EDGE",EDGE,{"disambiguationData":[OSD([sQuery(id+"F9.wireOp",EDGE,"E89"),sQuery(id+"F9.wireOp",EDGE,"E93")])]});
            var Q139;
            Q139=makeQuery(id+"F29.opExtrude","SWEPT_EDGE",EDGE,{"disambiguationData":[OSD([sQuery(id+"F8.wireOp",EDGE,"E77"),sQuery(id+"F8.wireOp",EDGE,"E81")])]});
            var Q140;
            Q140=makeQuery(id+"F29.opExtrude","SWEPT_EDGE",EDGE,{"disambiguationData":[OSD([sQuery(id+"F7.wireOp",EDGE,"E65"),sQuery(id+"F7.wireOp",EDGE,"E69")])]});
            var Q141;
            Q141=makeQuery(id+"F29.opExtrude","SWEPT_EDGE",EDGE,{"disambiguationData":[OSD([sQuery(id+"F27.wireOp",EDGE,"E305"),sQuery(id+"F27.wireOp",EDGE,"E309")])]});
            var Q142;
            Q142=makeQuery(id+"F29.opExtrude","SWEPT_EDGE",EDGE,{"disambiguationData":[OSD([sQuery(id+"F16.wireOp",EDGE,"E173"),sQuery(id+"F16.wireOp",EDGE,"E177")])]});
            var Q143;
            Q143=makeQuery(id+"F29.opExtrude","SWEPT_EDGE",EDGE,{"disambiguationData":[OSD([sQuery(id+"F15.wireOp",EDGE,"E161"),sQuery(id+"F15.wireOp",EDGE,"E165")])]});
            var Q144;
            Q144=makeQuery(id+"F29.opExtrude","SWEPT_EDGE",EDGE,{"disambiguationData":[OSD([sQuery(id+"F14.wireOp",EDGE,"E149"),sQuery(id+"F14.wireOp",EDGE,"E153")])]});
            var Q145;
            Q145=makeQuery(id+"F29.opExtrude","SWEPT_EDGE",EDGE,{"disambiguationData":[OSD([sQuery(id+"F13.wireOp",EDGE,"E137"),sQuery(id+"F13.wireOp",EDGE,"E141")])]});
            var Q146;
            Q146=makeQuery(id+"F29.opExtrude","SWEPT_EDGE",EDGE,{"disambiguationData":[OSD([sQuery(id+"F12.wireOp",EDGE,"E125"),sQuery(id+"F12.wireOp",EDGE,"E129")])]});
            var Q147;
            Q147=makeQuery(id+"F29.opExtrude","SWEPT_EDGE",EDGE,{"disambiguationData":[OSD([sQuery(id+"F17.wireOp",EDGE,"E185"),sQuery(id+"F17.wireOp",EDGE,"E189")])]});
            var Q148;
            Q148=makeQuery(id+"F29.opExtrude","SWEPT_EDGE",EDGE,{"disambiguationData":[OSD([sQuery(id+"F18.wireOp",EDGE,"E197"),sQuery(id+"F18.wireOp",EDGE,"E201")])]});
            var Q149;
            Q149=makeQuery(id+"F29.opExtrude","SWEPT_EDGE",EDGE,{"disambiguationData":[OSD([sQuery(id+"F22.wireOp",EDGE,"E245"),sQuery(id+"F22.wireOp",EDGE,"E249")])]});
            var Q150;
            Q150=makeQuery(id+"F29.opExtrude","SWEPT_EDGE",EDGE,{"disambiguationData":[OSD([sQuery(id+"F23.wireOp",EDGE,"E257"),sQuery(id+"F23.wireOp",EDGE,"E261")])]});
            var Q151;
            Q151=makeQuery(id+"F29.opExtrude","SWEPT_EDGE",EDGE,{"disambiguationData":[OSD([sQuery(id+"F19.wireOp",EDGE,"E209"),sQuery(id+"F19.wireOp",EDGE,"E213")])]});
            var Q152;
            Q152=makeQuery(id+"F29.opExtrude","SWEPT_EDGE",EDGE,{"disambiguationData":[OSD([sQuery(id+"F25.wireOp",EDGE,"E281"),sQuery(id+"F25.wireOp",EDGE,"E285")])]});
            var Q153;
            Q153=makeQuery(id+"F29.opExtrude","SWEPT_EDGE",EDGE,{"disambiguationData":[OSD([sQuery(id+"F26.wireOp",EDGE,"E293"),sQuery(id+"F26.wireOp",EDGE,"E297")])]});
            var Q154;
            Q154=makeQuery(id+"F29.opExtrude","SWEPT_EDGE",EDGE,{"disambiguationData":[OSD([sQuery(id+"F3.wireOp",EDGE,"E17"),sQuery(id+"F3.wireOp",EDGE,"E18")])]});
            var Q155;
            Q155=makeQuery(id+"F29.opExtrude","SWEPT_EDGE",EDGE,{"disambiguationData":[OSD([sQuery(id+"F4.wireOp",EDGE,"E29"),sQuery(id+"F4.wireOp",EDGE,"E30")])]});
            var Q156;
            Q156=makeQuery(id+"F29.opExtrude","SWEPT_EDGE",EDGE,{"disambiguationData":[OSD([sQuery(id+"F5.wireOp",EDGE,"E41"),sQuery(id+"F5.wireOp",EDGE,"E42")])]});
            var Q157;
            Q157=makeQuery(id+"F29.opExtrude","SWEPT_EDGE",EDGE,{"disambiguationData":[OSD([sQuery(id+"F6.wireOp",EDGE,"E53"),sQuery(id+"F6.wireOp",EDGE,"E54")])]});
            var Q158;
            Q158=makeQuery(id+"F29.opExtrude","SWEPT_EDGE",EDGE,{"disambiguationData":[OSD([sQuery(id+"F11.wireOp",EDGE,"E113"),sQuery(id+"F11.wireOp",EDGE,"E114")])]});
            var Q159;
            Q159=makeQuery(id+"F29.opExtrude","SWEPT_EDGE",EDGE,{"disambiguationData":[OSD([sQuery(id+"F10.wireOp",EDGE,"E101"),sQuery(id+"F10.wireOp",EDGE,"E102")])]});
            var Q160;
            Q160=makeQuery(id+"F29.opExtrude","SWEPT_EDGE",EDGE,{"disambiguationData":[OSD([sQuery(id+"F9.wireOp",EDGE,"E89"),sQuery(id+"F9.wireOp",EDGE,"E90")])]});
            var Q161;
            Q161=makeQuery(id+"F29.opExtrude","SWEPT_EDGE",EDGE,{"disambiguationData":[OSD([sQuery(id+"F8.wireOp",EDGE,"E77"),sQuery(id+"F8.wireOp",EDGE,"E78")])]});
            var Q162;
            Q162=makeQuery(id+"F29.opExtrude","SWEPT_EDGE",EDGE,{"disambiguationData":[OSD([sQuery(id+"F7.wireOp",EDGE,"E65"),sQuery(id+"F7.wireOp",EDGE,"E66")])]});
            var Q163;
            Q163=makeQuery(id+"F29.opExtrude","SWEPT_EDGE",EDGE,{"disambiguationData":[OSD([sQuery(id+"F27.wireOp",EDGE,"E305"),sQuery(id+"F27.wireOp",EDGE,"E306")])]});
            var Q164;
            Q164=makeQuery(id+"F29.opExtrude","SWEPT_EDGE",EDGE,{"disambiguationData":[OSD([sQuery(id+"F16.wireOp",EDGE,"E173"),sQuery(id+"F16.wireOp",EDGE,"E174")])]});
            var Q165;
            Q165=makeQuery(id+"F29.opExtrude","SWEPT_EDGE",EDGE,{"disambiguationData":[OSD([sQuery(id+"F15.wireOp",EDGE,"E161"),sQuery(id+"F15.wireOp",EDGE,"E162")])]});
            var Q166;
            Q166=makeQuery(id+"F29.opExtrude","SWEPT_EDGE",EDGE,{"disambiguationData":[OSD([sQuery(id+"F13.wireOp",EDGE,"E137"),sQuery(id+"F13.wireOp",EDGE,"E138")])]});
            var Q167;
            Q167=makeQuery(id+"F29.opExtrude","SWEPT_EDGE",EDGE,{"disambiguationData":[OSD([sQuery(id+"F12.wireOp",EDGE,"E125"),sQuery(id+"F12.wireOp",EDGE,"E126")])]});
            var Q168;
            Q168=makeQuery(id+"F29.opExtrude","SWEPT_EDGE",EDGE,{"disambiguationData":[OSD([sQuery(id+"F14.wireOp",EDGE,"E149"),sQuery(id+"F14.wireOp",EDGE,"E150")])]});
            var Q169;
            Q169=makeQuery(id+"F29.opExtrude","SWEPT_EDGE",EDGE,{"disambiguationData":[OSD([sQuery(id+"F17.wireOp",EDGE,"E185"),sQuery(id+"F17.wireOp",EDGE,"E186")])]});
            var Q170;
            Q170=makeQuery(id+"F29.opExtrude","SWEPT_EDGE",EDGE,{"disambiguationData":[OSD([sQuery(id+"F18.wireOp",EDGE,"E197"),sQuery(id+"F18.wireOp",EDGE,"E198")])]});
            var Q171;
            Q171=makeQuery(id+"F29.opExtrude","SWEPT_EDGE",EDGE,{"disambiguationData":[OSD([sQuery(id+"F19.wireOp",EDGE,"E209"),sQuery(id+"F19.wireOp",EDGE,"E210")])]});
            var Q172;
            Q172=makeQuery(id+"F29.opExtrude","SWEPT_EDGE",EDGE,{"disambiguationData":[OSD([sQuery(id+"F20.wireOp",EDGE,"E221"),sQuery(id+"F20.wireOp",EDGE,"E222")])]});
            var Q173;
            Q173=makeQuery(id+"F29.opExtrude","SWEPT_EDGE",EDGE,{"disambiguationData":[OSD([sQuery(id+"F21.wireOp",EDGE,"E233"),sQuery(id+"F21.wireOp",EDGE,"E234")])]});
            var Q174;
            Q174=makeQuery(id+"F29.opExtrude","SWEPT_EDGE",EDGE,{"disambiguationData":[OSD([sQuery(id+"F23.wireOp",EDGE,"E257"),sQuery(id+"F23.wireOp",EDGE,"E258")])]});
            var Q175;
            Q175=makeQuery(id+"F29.opExtrude","SWEPT_EDGE",EDGE,{"disambiguationData":[OSD([sQuery(id+"F25.wireOp",EDGE,"E281"),sQuery(id+"F25.wireOp",EDGE,"E282")])]});
            var Q176;
            Q176=makeQuery(id+"F29.opExtrude","SWEPT_EDGE",EDGE,{"disambiguationData":[OSD([sQuery(id+"F26.wireOp",EDGE,"E293"),sQuery(id+"F26.wireOp",EDGE,"E294")])]});
            var Q177;
            Q177=makeQuery(id+"F29.opExtrude","SWEPT_EDGE",EDGE,{"disambiguationData":[OSD([sQuery(id+"F3.wireOp",EDGE,"E20"),sQuery(id+"F3.wireOp",EDGE,"E21")])]});
            var Q178;
            Q178=makeQuery(id+"F29.opExtrude","SWEPT_EDGE",EDGE,{"disambiguationData":[OSD([sQuery(id+"F4.wireOp",EDGE,"E32"),sQuery(id+"F4.wireOp",EDGE,"E33")])]});
            var Q179;
            Q179=makeQuery(id+"F29.opExtrude","SWEPT_EDGE",EDGE,{"disambiguationData":[OSD([sQuery(id+"F5.wireOp",EDGE,"E44"),sQuery(id+"F5.wireOp",EDGE,"E45")])]});
            var Q180;
            Q180=makeQuery(id+"F29.opExtrude","SWEPT_EDGE",EDGE,{"disambiguationData":[OSD([sQuery(id+"F6.wireOp",EDGE,"E56"),sQuery(id+"F6.wireOp",EDGE,"E57")])]});
            var Q181;
            Q181=makeQuery(id+"F29.opExtrude","SWEPT_EDGE",EDGE,{"disambiguationData":[OSD([sQuery(id+"F6.wireOp",EDGE,"E54"),sQuery(id+"F6.wireOp",EDGE,"E55")])]});
            var Q182;
            Q182=makeQuery(id+"F29.opExtrude","SWEPT_EDGE",EDGE,{"disambiguationData":[OSD([sQuery(id+"F5.wireOp",EDGE,"E42"),sQuery(id+"F5.wireOp",EDGE,"E43")])]});
            var Q183;
            Q183=makeQuery(id+"F29.opExtrude","SWEPT_EDGE",EDGE,{"disambiguationData":[OSD([sQuery(id+"F4.wireOp",EDGE,"E30"),sQuery(id+"F4.wireOp",EDGE,"E31")])]});
            var Q184;
            Q184=makeQuery(id+"F29.opExtrude","SWEPT_EDGE",EDGE,{"disambiguationData":[OSD([sQuery(id+"F3.wireOp",EDGE,"E18"),sQuery(id+"F3.wireOp",EDGE,"E19")])]});
            var Q185;
            Q185=makeQuery(id+"F29.opExtrude","SWEPT_EDGE",EDGE,{"disambiguationData":[OSD([sQuery(id+"F7.wireOp",EDGE,"E66"),sQuery(id+"F7.wireOp",EDGE,"E67")])]});
            var Q186;
            Q186=makeQuery(id+"F29.opExtrude","SWEPT_EDGE",EDGE,{"disambiguationData":[OSD([sQuery(id+"F8.wireOp",EDGE,"E78"),sQuery(id+"F8.wireOp",EDGE,"E79")])]});
            var Q187;
            Q187=makeQuery(id+"F29.opExtrude","SWEPT_EDGE",EDGE,{"disambiguationData":[OSD([sQuery(id+"F9.wireOp",EDGE,"E90"),sQuery(id+"F9.wireOp",EDGE,"E91")])]});
            var Q188;
            Q188=makeQuery(id+"F29.opExtrude","SWEPT_EDGE",EDGE,{"disambiguationData":[OSD([sQuery(id+"F10.wireOp",EDGE,"E102"),sQuery(id+"F10.wireOp",EDGE,"E103")])]});
            var Q189;
            Q189=makeQuery(id+"F29.opExtrude","SWEPT_EDGE",EDGE,{"disambiguationData":[OSD([sQuery(id+"F11.wireOp",EDGE,"E114"),sQuery(id+"F11.wireOp",EDGE,"E115")])]});
            var Q190;
            Q190=makeQuery(id+"F29.opExtrude","SWEPT_EDGE",EDGE,{"disambiguationData":[OSD([sQuery(id+"F7.wireOp",EDGE,"E68"),sQuery(id+"F7.wireOp",EDGE,"E69")])]});
            var Q191;
            Q191=makeQuery(id+"F29.opExtrude","SWEPT_EDGE",EDGE,{"disambiguationData":[OSD([sQuery(id+"F8.wireOp",EDGE,"E80"),sQuery(id+"F8.wireOp",EDGE,"E81")])]});
            var Q192;
            Q192=makeQuery(id+"F29.opExtrude","SWEPT_EDGE",EDGE,{"disambiguationData":[OSD([sQuery(id+"F9.wireOp",EDGE,"E92"),sQuery(id+"F9.wireOp",EDGE,"E93")])]});
            var Q193;
            Q193=makeQuery(id+"F29.opExtrude","SWEPT_EDGE",EDGE,{"disambiguationData":[OSD([sQuery(id+"F10.wireOp",EDGE,"E104"),sQuery(id+"F10.wireOp",EDGE,"E105")])]});
            var Q194;
            Q194=makeQuery(id+"F29.opExtrude","SWEPT_EDGE",EDGE,{"disambiguationData":[OSD([sQuery(id+"F11.wireOp",EDGE,"E116"),sQuery(id+"F11.wireOp",EDGE,"E117")])]});
            var Q195;
            Q195=makeQuery(id+"F29.opExtrude","SWEPT_EDGE",EDGE,{"disambiguationData":[OSD([sQuery(id+"F27.wireOp",EDGE,"E308"),sQuery(id+"F27.wireOp",EDGE,"E309")])]});
            var Q196;
            Q196=makeQuery(id+"F29.opExtrude","SWEPT_EDGE",EDGE,{"disambiguationData":[OSD([sQuery(id+"F16.wireOp",EDGE,"E176"),sQuery(id+"F16.wireOp",EDGE,"E177")])]});
            var Q197;
            Q197=makeQuery(id+"F29.opExtrude","SWEPT_EDGE",EDGE,{"disambiguationData":[OSD([sQuery(id+"F15.wireOp",EDGE,"E164"),sQuery(id+"F15.wireOp",EDGE,"E165")])]});
            var Q198;
            Q198=makeQuery(id+"F29.opExtrude","SWEPT_EDGE",EDGE,{"disambiguationData":[OSD([sQuery(id+"F14.wireOp",EDGE,"E152"),sQuery(id+"F14.wireOp",EDGE,"E153")])]});
            var Q199;
            Q199=makeQuery(id+"F29.opExtrude","SWEPT_EDGE",EDGE,{"disambiguationData":[OSD([sQuery(id+"F13.wireOp",EDGE,"E140"),sQuery(id+"F13.wireOp",EDGE,"E141")])]});
            var Q200;
            Q200=makeQuery(id+"F29.opExtrude","SWEPT_EDGE",EDGE,{"disambiguationData":[OSD([sQuery(id+"F12.wireOp",EDGE,"E128"),sQuery(id+"F12.wireOp",EDGE,"E129")])]});
            var Q201;
            Q201=makeQuery(id+"F29.opExtrude","SWEPT_EDGE",EDGE,{"disambiguationData":[OSD([sQuery(id+"F12.wireOp",EDGE,"E126"),sQuery(id+"F12.wireOp",EDGE,"E127")])]});
            var Q202;
            Q202=makeQuery(id+"F29.opExtrude","SWEPT_EDGE",EDGE,{"disambiguationData":[OSD([sQuery(id+"F13.wireOp",EDGE,"E138"),sQuery(id+"F13.wireOp",EDGE,"E139")])]});
            var Q203;
            Q203=makeQuery(id+"F29.opExtrude","SWEPT_EDGE",EDGE,{"disambiguationData":[OSD([sQuery(id+"F14.wireOp",EDGE,"E150"),sQuery(id+"F14.wireOp",EDGE,"E151")])]});
            var Q204;
            Q204=makeQuery(id+"F29.opExtrude","SWEPT_EDGE",EDGE,{"disambiguationData":[OSD([sQuery(id+"F15.wireOp",EDGE,"E162"),sQuery(id+"F15.wireOp",EDGE,"E163")])]});
            var Q205;
            Q205=makeQuery(id+"F29.opExtrude","SWEPT_EDGE",EDGE,{"disambiguationData":[OSD([sQuery(id+"F16.wireOp",EDGE,"E174"),sQuery(id+"F16.wireOp",EDGE,"E175")])]});
            var Q206;
            Q206=makeQuery(id+"F29.opExtrude","SWEPT_EDGE",EDGE,{"disambiguationData":[OSD([sQuery(id+"F27.wireOp",EDGE,"E306"),sQuery(id+"F27.wireOp",EDGE,"E307")])]});
            var Q207;
            Q207=makeQuery(id+"F29.opExtrude","SWEPT_EDGE",EDGE,{"disambiguationData":[OSD([sQuery(id+"F21.wireOp",EDGE,"E234"),sQuery(id+"F21.wireOp",EDGE,"E235")])]});
            var Q208;
            Q208=makeQuery(id+"F29.opExtrude","SWEPT_EDGE",EDGE,{"disambiguationData":[OSD([sQuery(id+"F20.wireOp",EDGE,"E222"),sQuery(id+"F20.wireOp",EDGE,"E223")])]});
            var Q209;
            Q209=makeQuery(id+"F29.opExtrude","SWEPT_EDGE",EDGE,{"disambiguationData":[OSD([sQuery(id+"F19.wireOp",EDGE,"E210"),sQuery(id+"F19.wireOp",EDGE,"E211")])]});
            var Q210;
            Q210=makeQuery(id+"F29.opExtrude","SWEPT_EDGE",EDGE,{"disambiguationData":[OSD([sQuery(id+"F18.wireOp",EDGE,"E198"),sQuery(id+"F18.wireOp",EDGE,"E199")])]});
            var Q211;
            Q211=makeQuery(id+"F29.opExtrude","SWEPT_EDGE",EDGE,{"disambiguationData":[OSD([sQuery(id+"F17.wireOp",EDGE,"E186"),sQuery(id+"F17.wireOp",EDGE,"E187")])]});
            var Q212;
            Q212=makeQuery(id+"F29.opExtrude","SWEPT_EDGE",EDGE,{"disambiguationData":[OSD([sQuery(id+"F17.wireOp",EDGE,"E188"),sQuery(id+"F17.wireOp",EDGE,"E189")])]});
            var Q213;
            Q213=makeQuery(id+"F29.opExtrude","SWEPT_EDGE",EDGE,{"disambiguationData":[OSD([sQuery(id+"F18.wireOp",EDGE,"E200"),sQuery(id+"F18.wireOp",EDGE,"E201")])]});
            var Q214;
            Q214=makeQuery(id+"F29.opExtrude","SWEPT_EDGE",EDGE,{"disambiguationData":[OSD([sQuery(id+"F19.wireOp",EDGE,"E212"),sQuery(id+"F19.wireOp",EDGE,"E213")])]});
            var Q215;
            Q215=makeQuery(id+"F29.opExtrude","SWEPT_EDGE",EDGE,{"disambiguationData":[OSD([sQuery(id+"F20.wireOp",EDGE,"E224"),sQuery(id+"F20.wireOp",EDGE,"E225")])]});
            var Q216;
            Q216=makeQuery(id+"F29.opExtrude","SWEPT_EDGE",EDGE,{"disambiguationData":[OSD([sQuery(id+"F21.wireOp",EDGE,"E236"),sQuery(id+"F21.wireOp",EDGE,"E237")])]});
            var Q217;
            Q217=makeQuery(id+"F29.opExtrude","SWEPT_EDGE",EDGE,{"disambiguationData":[OSD([sQuery(id+"F26.wireOp",EDGE,"E296"),sQuery(id+"F26.wireOp",EDGE,"E297")])]});
            var Q218;
            Q218=makeQuery(id+"F29.opExtrude","SWEPT_EDGE",EDGE,{"disambiguationData":[OSD([sQuery(id+"F25.wireOp",EDGE,"E284"),sQuery(id+"F25.wireOp",EDGE,"E285")])]});
            var Q219;
            Q219=makeQuery(id+"F29.opExtrude","SWEPT_EDGE",EDGE,{"disambiguationData":[OSD([sQuery(id+"F24.wireOp",EDGE,"E272"),sQuery(id+"F24.wireOp",EDGE,"E273")])]});
            var Q220;
            Q220=makeQuery(id+"F29.opExtrude","SWEPT_EDGE",EDGE,{"disambiguationData":[OSD([sQuery(id+"F22.wireOp",EDGE,"E248"),sQuery(id+"F22.wireOp",EDGE,"E249")])]});
            var Q221;
            Q221=makeQuery(id+"F29.opExtrude","SWEPT_EDGE",EDGE,{"disambiguationData":[OSD([sQuery(id+"F23.wireOp",EDGE,"E260"),sQuery(id+"F23.wireOp",EDGE,"E261")])]});
            var Q222;
            Q222=makeQuery(id+"F29.opExtrude","SWEPT_EDGE",EDGE,{"disambiguationData":[OSD([sQuery(id+"F22.wireOp",EDGE,"E245"),sQuery(id+"F22.wireOp",EDGE,"E246")])]});
            var Q223;
            Q223=makeQuery(id+"F29.opExtrude","SWEPT_EDGE",EDGE,{"disambiguationData":[OSD([sQuery(id+"F22.wireOp",EDGE,"E246"),sQuery(id+"F22.wireOp",EDGE,"E247")])]});
            var Q224;
            Q224=makeQuery(id+"F29.opExtrude","SWEPT_EDGE",EDGE,{"disambiguationData":[OSD([sQuery(id+"F23.wireOp",EDGE,"E258"),sQuery(id+"F23.wireOp",EDGE,"E259")])]});
            var Q225;
            Q225=makeQuery(id+"F29.opExtrude","SWEPT_EDGE",EDGE,{"disambiguationData":[OSD([sQuery(id+"F24.wireOp",EDGE,"E270"),sQuery(id+"F24.wireOp",EDGE,"E271")])]});
            var Q226;
            Q226=makeQuery(id+"F29.opExtrude","SWEPT_EDGE",EDGE,{"disambiguationData":[OSD([sQuery(id+"F25.wireOp",EDGE,"E282"),sQuery(id+"F25.wireOp",EDGE,"E283")])]});
            var Q227;
            Q227=makeQuery(id+"F29.opExtrude","SWEPT_EDGE",EDGE,{"disambiguationData":[OSD([sQuery(id+"F26.wireOp",EDGE,"E294"),sQuery(id+"F26.wireOp",EDGE,"E295")])]});
            var Q228;
            Q228=makeQuery(id+"F29.opExtrude","SWEPT_EDGE",EDGE,{"disambiguationData":[OSD([sQuery(id+"F3.wireOp",EDGE,"E19"),sQuery(id+"F3.wireOp",EDGE,"E20")])]});
            var Q229;
            Q229=makeQuery(id+"F29.opExtrude","SWEPT_EDGE",EDGE,{"disambiguationData":[OSD([sQuery(id+"F4.wireOp",EDGE,"E31"),sQuery(id+"F4.wireOp",EDGE,"E32")])]});
            var Q230;
            Q230=makeQuery(id+"F29.opExtrude","SWEPT_EDGE",EDGE,{"disambiguationData":[OSD([sQuery(id+"F5.wireOp",EDGE,"E43"),sQuery(id+"F5.wireOp",EDGE,"E44")])]});
            var Q231;
            Q231=makeQuery(id+"F29.opExtrude","SWEPT_EDGE",EDGE,{"disambiguationData":[OSD([sQuery(id+"F6.wireOp",EDGE,"E55"),sQuery(id+"F6.wireOp",EDGE,"E56")])]});
            var Q232;
            Q232=makeQuery(id+"F29.opExtrude","SWEPT_EDGE",EDGE,{"disambiguationData":[OSD([sQuery(id+"F11.wireOp",EDGE,"E115"),sQuery(id+"F11.wireOp",EDGE,"E116")])]});
            var Q233;
            Q233=makeQuery(id+"F29.opExtrude","SWEPT_EDGE",EDGE,{"disambiguationData":[OSD([sQuery(id+"F10.wireOp",EDGE,"E103"),sQuery(id+"F10.wireOp",EDGE,"E104")])]});
            var Q234;
            Q234=makeQuery(id+"F29.opExtrude","SWEPT_EDGE",EDGE,{"disambiguationData":[OSD([sQuery(id+"F9.wireOp",EDGE,"E91"),sQuery(id+"F9.wireOp",EDGE,"E92")])]});
            var Q235;
            Q235=makeQuery(id+"F29.opExtrude","SWEPT_EDGE",EDGE,{"disambiguationData":[OSD([sQuery(id+"F8.wireOp",EDGE,"E79"),sQuery(id+"F8.wireOp",EDGE,"E80")])]});
            var Q236;
            Q236=makeQuery(id+"F29.opExtrude","SWEPT_EDGE",EDGE,{"disambiguationData":[OSD([sQuery(id+"F7.wireOp",EDGE,"E67"),sQuery(id+"F7.wireOp",EDGE,"E68")])]});
            var Q237;
            Q237=makeQuery(id+"F29.opExtrude","SWEPT_EDGE",EDGE,{"disambiguationData":[OSD([sQuery(id+"F12.wireOp",EDGE,"E127"),sQuery(id+"F12.wireOp",EDGE,"E128")])]});
            var Q238;
            Q238=makeQuery(id+"F29.opExtrude","SWEPT_EDGE",EDGE,{"disambiguationData":[OSD([sQuery(id+"F13.wireOp",EDGE,"E139"),sQuery(id+"F13.wireOp",EDGE,"E140")])]});
            var Q239;
            Q239=makeQuery(id+"F29.opExtrude","SWEPT_EDGE",EDGE,{"disambiguationData":[OSD([sQuery(id+"F14.wireOp",EDGE,"E151"),sQuery(id+"F14.wireOp",EDGE,"E152")])]});
            var Q240;
            Q240=makeQuery(id+"F29.opExtrude","SWEPT_EDGE",EDGE,{"disambiguationData":[OSD([sQuery(id+"F15.wireOp",EDGE,"E163"),sQuery(id+"F15.wireOp",EDGE,"E164")])]});
            var Q241;
            Q241=makeQuery(id+"F29.opExtrude","SWEPT_EDGE",EDGE,{"disambiguationData":[OSD([sQuery(id+"F16.wireOp",EDGE,"E175"),sQuery(id+"F16.wireOp",EDGE,"E176")])]});
            var Q242;
            Q242=makeQuery(id+"F29.opExtrude","SWEPT_EDGE",EDGE,{"disambiguationData":[OSD([sQuery(id+"F27.wireOp",EDGE,"E307"),sQuery(id+"F27.wireOp",EDGE,"E308")])]});
            var Q243;
            Q243=makeQuery(id+"F29.opExtrude","SWEPT_EDGE",EDGE,{"disambiguationData":[OSD([sQuery(id+"F17.wireOp",EDGE,"E187"),sQuery(id+"F17.wireOp",EDGE,"E188")])]});
            var Q244;
            Q244=makeQuery(id+"F29.opExtrude","SWEPT_EDGE",EDGE,{"disambiguationData":[OSD([sQuery(id+"F18.wireOp",EDGE,"E199"),sQuery(id+"F18.wireOp",EDGE,"E200")])]});
            var Q245;
            Q245=makeQuery(id+"F29.opExtrude","SWEPT_EDGE",EDGE,{"disambiguationData":[OSD([sQuery(id+"F19.wireOp",EDGE,"E211"),sQuery(id+"F19.wireOp",EDGE,"E212")])]});
            var Q246;
            Q246=makeQuery(id+"F29.opExtrude","SWEPT_EDGE",EDGE,{"disambiguationData":[OSD([sQuery(id+"F20.wireOp",EDGE,"E223"),sQuery(id+"F20.wireOp",EDGE,"E224")])]});
            var Q247;
            Q247=makeQuery(id+"F29.opExtrude","SWEPT_EDGE",EDGE,{"disambiguationData":[OSD([sQuery(id+"F21.wireOp",EDGE,"E235"),sQuery(id+"F21.wireOp",EDGE,"E236")])]});
            var Q248;
            Q248=makeQuery(id+"F29.opExtrude","SWEPT_EDGE",EDGE,{"disambiguationData":[OSD([sQuery(id+"F26.wireOp",EDGE,"E295"),sQuery(id+"F26.wireOp",EDGE,"E296")])]});
            var Q249;
            Q249=makeQuery(id+"F29.opExtrude","SWEPT_EDGE",EDGE,{"disambiguationData":[OSD([sQuery(id+"F25.wireOp",EDGE,"E283"),sQuery(id+"F25.wireOp",EDGE,"E284")])]});
            var Q250;
            Q250=makeQuery(id+"F29.opExtrude","SWEPT_EDGE",EDGE,{"disambiguationData":[OSD([sQuery(id+"F24.wireOp",EDGE,"E271"),sQuery(id+"F24.wireOp",EDGE,"E272")])]});
            var Q251;
            Q251=makeQuery(id+"F29.opExtrude","SWEPT_EDGE",EDGE,{"disambiguationData":[OSD([sQuery(id+"F23.wireOp",EDGE,"E259"),sQuery(id+"F23.wireOp",EDGE,"E260")])]});
            var Q252;
            Q252=makeQuery(id+"F29.opExtrude","SWEPT_EDGE",EDGE,{"disambiguationData":[OSD([sQuery(id+"F22.wireOp",EDGE,"E247"),sQuery(id+"F22.wireOp",EDGE,"E248")])]});
            fillet(context, id + "F31", {"entities" : qUnion([Q0, Q1, Q2, Q3, Q4, Q5, Q6, Q7, Q8, Q9, Q10, Q11, Q12, Q13, Q14, Q15, Q16, Q17, Q18, Q19, Q20, Q21, Q22, Q23, Q24, Q25, Q26, Q27, Q28, Q29, Q30, Q31, Q32, Q33, Q34, Q35, Q36, Q37, Q38, Q39, Q40, Q41, Q42, Q43, Q44, Q45, Q46, Q47, Q48, Q49, Q50, Q51, Q52, Q53, Q54, Q55, Q56, Q57, Q58, Q59, Q60, Q61, Q62, Q63, Q64, Q65, Q66, Q67, Q68, Q69, Q70, Q71, Q72, Q73, Q74, Q75, Q76, Q77, Q78, Q79, Q80, Q81, Q82, Q83, Q84, Q85, Q86, Q87, Q88, Q89, Q90, Q91, Q92, Q93, Q94, Q95, Q96, Q97, Q98, Q99, Q100, Q101, Q102, Q103, Q104, Q105, Q106, Q107, Q108, Q109, Q110, Q111, Q112, Q113, Q114, Q115, Q116, Q117, Q118, Q119, Q120, Q121, Q122, Q123, Q124, Q125, Q126, Q127, Q128, Q129, Q130, Q131, Q132, Q133, Q134, Q135, Q136, Q137, Q138, Q139, Q140, Q141, Q142, Q143, Q144, Q145, Q146, Q147, Q148, Q149, Q150, Q151, Q152, Q153, Q154, Q155, Q156, Q157, Q158, Q159, Q160, Q161, Q162, Q163, Q164, Q165, Q166, Q167, Q168, Q169, Q170, Q171, Q172, Q173, Q174, Q175, Q176, Q177, Q178, Q179, Q180, Q181, Q182, Q183, Q184, Q185, Q186, Q187, Q188, Q189, Q190, Q191, Q192, Q193, Q194, Q195, Q196, Q197, Q198, Q199, Q200, Q201, Q202, Q203, Q204, Q205, Q206, Q207, Q208, Q209, Q210, Q211, Q212, Q213, Q214, Q215, Q216, Q217, Q218, Q219, Q220, Q221, Q222, Q223, Q224, Q225, Q226, Q227, Q228, Q229, Q230, Q231, Q232, Q233, Q234, Q235, Q236, Q237, Q238, Q239, Q240, Q241, Q242, Q243, Q244, Q245, Q246, Q247, Q248, Q249, Q250, Q251, Q252]), "radius" : 2 * mm, "tangentPropagation" : true, "allowEdgeOverflow" : false});
        }
    });
